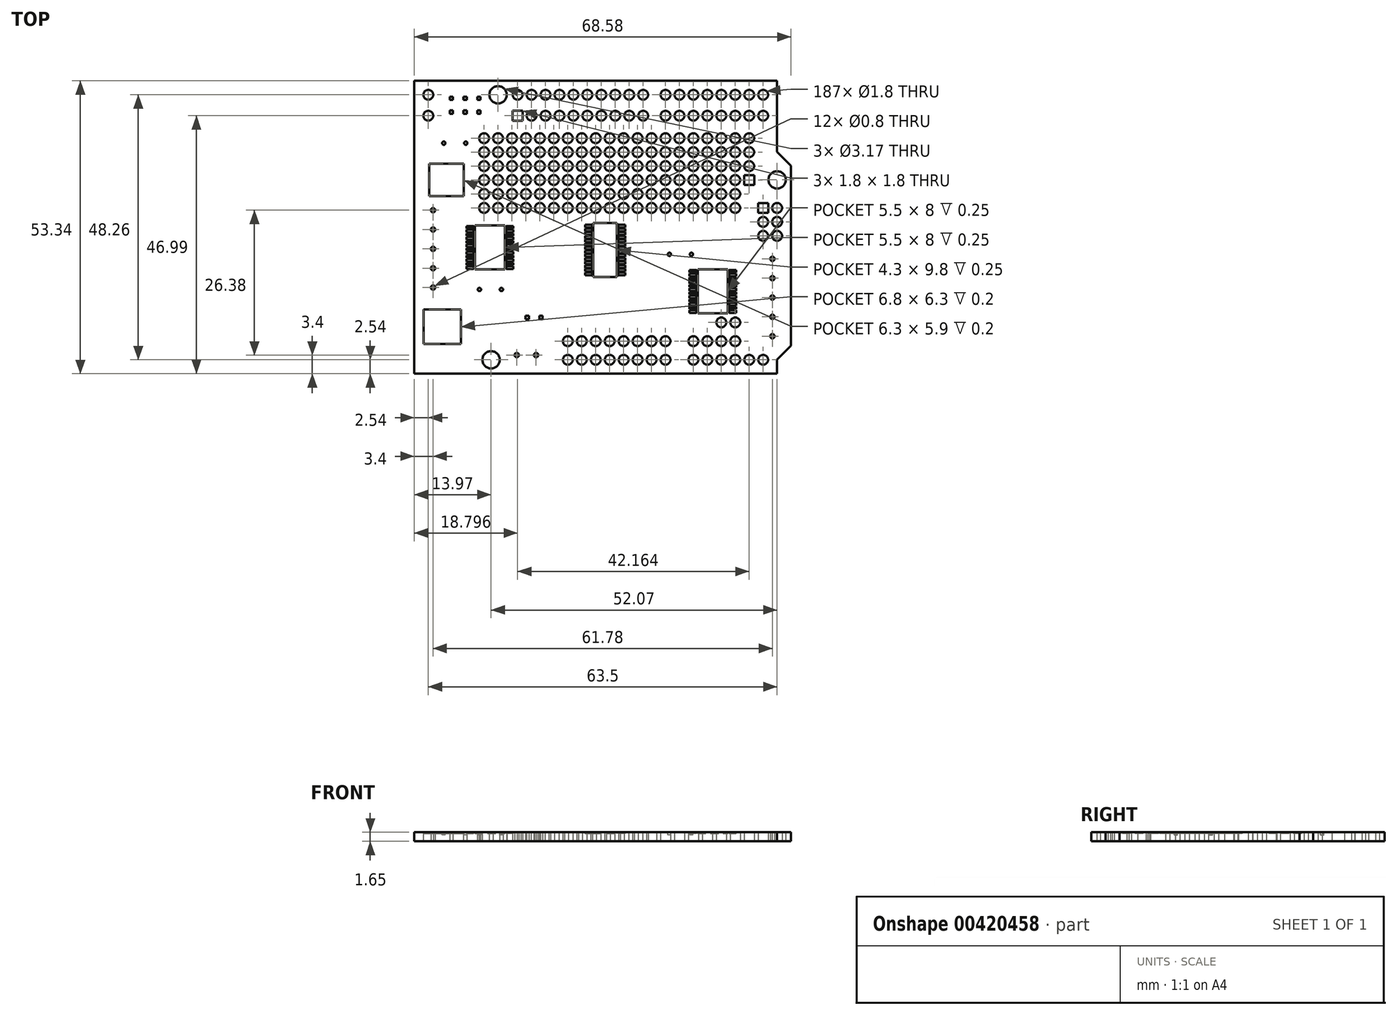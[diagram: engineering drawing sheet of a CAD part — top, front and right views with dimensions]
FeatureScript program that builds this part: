
annotation { "Feature Type Name" : "Feature", "Feature Type Description" : "" }
export const myFeature = defineFeature(function(context is Context, id is Id, definition is map)
    precondition{}
    {
        {
            var Q0;
            Q0=qCreatedBy(makeId("Top.planeOp"),FACE);
            var sketch = newSketch(context, id + "F0", { "sketchPlane" : qUnion([Q0])});
            skLineSegment(sketch, "E0.bottom", {"start": v(0, 0) * mm, "end": v(66.04, 0) * mm});
            skLineSegment(sketch, "E0.top", {"start": v(0, 53.34) * mm, "end": v(66.04, 53.34) * mm});
            skLineSegment(sketch, "E0.left", {"start": v(0, 0) * mm, "end": v(0, 53.34) * mm});
            skLineSegment(sketch, "E0.right", {"start": v(66.04, 0) * mm, "end": v(66.04, 2.54) * mm});
            skLineSegment(sketch, "E1", {"start": v(66.04, 40.39) * mm, "end": v(68.58, 37.85) * mm});
            skLineSegment(sketch, "E2", {"start": v(68.58, 37.85) * mm, "end": v(68.58, 5.08) * mm});
            skLineSegment(sketch, "E3", {"start": v(68.58, 5.08) * mm, "end": v(66.04, 2.54) * mm});
            skLineSegment(sketch, "E4.trimOffspring", {"start": v(66.04, 40.39) * mm, "end": v(66.04, 53.34) * mm});
            skCircle(sketch, "E5", {"center": v(15.24, 50.8) * mm, "radius": 1.59 * mm});
            skCircle(sketch, "E6", {"center": v(13.97, 2.54) * mm, "radius": 1.59 * mm});
            skCircle(sketch, "E7", {"center": v(66.04, 35.3) * mm, "radius": 1.59 * mm});
            skLineSegment(sketch, "E8", {"start": v(0, 50.8) * mm, "end": v(66.04, 50.8) * mm, "construction": true});
            skCircle(sketch, "E9", {"center": v(63.5, 50.8) * mm, "radius": 0.9 * mm});
            skCircle(sketch, "E10.1.0.0", {"center": v(60.96, 50.8) * mm, "radius": 0.9 * mm});
            skCircle(sketch, "E10.2.0.0", {"center": v(58.42, 50.8) * mm, "radius": 0.9 * mm});
            skCircle(sketch, "E10.3.0.0", {"center": v(55.88, 50.8) * mm, "radius": 0.9 * mm});
            skCircle(sketch, "E10.4.0.0", {"center": v(53.34, 50.8) * mm, "radius": 0.9 * mm});
            skCircle(sketch, "E10.5.0.0", {"center": v(50.8, 50.8) * mm, "radius": 0.9 * mm});
            skCircle(sketch, "E10.6.0.0", {"center": v(48.26, 50.8) * mm, "radius": 0.9 * mm});
            skCircle(sketch, "E10.7.0.0", {"center": v(45.72, 50.8) * mm, "radius": 0.9 * mm});
            skLineSegment(sketch, "E10.direction1", {"start": v(63.5, 50.8) * mm, "end": v(60.96, 50.8) * mm, "construction": true});
            skCircle(sketch, "E11", {"center": v(41.66, 50.8) * mm, "radius": 0.9 * mm});
            skCircle(sketch, "E12.1.0.0", {"center": v(39.12, 50.8) * mm, "radius": 0.9 * mm});
            skCircle(sketch, "E12.2.0.0", {"center": v(36.58, 50.8) * mm, "radius": 0.9 * mm});
            skCircle(sketch, "E12.3.0.0", {"center": v(34.04, 50.8) * mm, "radius": 0.9 * mm});
            skCircle(sketch, "E12.4.0.0", {"center": v(31.5, 50.8) * mm, "radius": 0.9 * mm});
            skCircle(sketch, "E12.5.0.0", {"center": v(28.96, 50.8) * mm, "radius": 0.9 * mm});
            skCircle(sketch, "E12.6.0.0", {"center": v(26.42, 50.8) * mm, "radius": 0.9 * mm});
            skCircle(sketch, "E12.7.0.0", {"center": v(23.88, 50.8) * mm, "radius": 0.9 * mm});
            skCircle(sketch, "E12.8.0.0", {"center": v(21.34, 50.8) * mm, "radius": 0.9 * mm});
            skCircle(sketch, "E12.9.0.0", {"center": v(18.8, 50.8) * mm, "radius": 0.9 * mm});
            skLineSegment(sketch, "E12.direction1", {"start": v(41.66, 50.8) * mm, "end": v(39.12, 50.8) * mm, "construction": true});
            skLineSegment(sketch, "E13", {"start": v(66.04, 2.54) * mm, "end": v(0, 2.54) * mm, "construction": true});
            skCircle(sketch, "E14", {"center": v(63.5, 2.54) * mm, "radius": 0.9 * mm});
            skCircle(sketch, "E15.1.0.0", {"center": v(60.96, 2.54) * mm, "radius": 0.9 * mm});
            skCircle(sketch, "E15.2.0.0", {"center": v(58.42, 2.54) * mm, "radius": 0.9 * mm});
            skCircle(sketch, "E15.3.0.0", {"center": v(55.88, 2.54) * mm, "radius": 0.9 * mm});
            skCircle(sketch, "E15.4.0.0", {"center": v(53.34, 2.54) * mm, "radius": 0.9 * mm});
            skCircle(sketch, "E15.5.0.0", {"center": v(50.8, 2.54) * mm, "radius": 0.9 * mm});
            skLineSegment(sketch, "E15.direction1", {"start": v(63.5, 2.54) * mm, "end": v(60.96, 2.54) * mm, "construction": true});
            skCircle(sketch, "E16", {"center": v(45.72, 2.54) * mm, "radius": 0.9 * mm});
            skCircle(sketch, "E17.1.0.0", {"center": v(43.18, 2.54) * mm, "radius": 0.9 * mm});
            skCircle(sketch, "E17.2.0.0", {"center": v(40.64, 2.54) * mm, "radius": 0.9 * mm});
            skCircle(sketch, "E17.3.0.0", {"center": v(38.1, 2.54) * mm, "radius": 0.9 * mm});
            skCircle(sketch, "E17.4.0.0", {"center": v(35.56, 2.54) * mm, "radius": 0.9 * mm});
            skCircle(sketch, "E17.5.0.0", {"center": v(33.02, 2.54) * mm, "radius": 0.9 * mm});
            skCircle(sketch, "E17.6.0.0", {"center": v(30.48, 2.54) * mm, "radius": 0.9 * mm});
            skCircle(sketch, "E17.7.0.0", {"center": v(27.94, 2.54) * mm, "radius": 0.9 * mm});
            skLineSegment(sketch, "E17.direction1", {"start": v(45.72, 2.54) * mm, "end": v(43.18, 2.54) * mm, "construction": true});
            skLineSegment(sketch, "E18", {"start": v(0, 46.99) * mm, "end": v(66.04, 46.99) * mm, "construction": true});
            skLineSegment(sketch, "E19.1.0.0", {"start": v(41.66, 46.99) * mm, "end": v(39.12, 46.99) * mm, "construction": true});
            skLineSegment(sketch, "E19.1.0.1", {"start": v(63.5, 46.99) * mm, "end": v(60.96, 46.99) * mm, "construction": true});
            skCircle(sketch, "E19.1.0.2", {"center": v(48.26, 46.99) * mm, "radius": 0.9 * mm});
            skCircle(sketch, "E19.1.0.3", {"center": v(31.5, 47) * mm, "radius": 0.9 * mm});
            skCircle(sketch, "E19.1.0.4", {"center": v(50.8, 46.99) * mm, "radius": 0.9 * mm});
            skCircle(sketch, "E19.1.0.6", {"center": v(34.04, 47) * mm, "radius": 0.9 * mm});
            skCircle(sketch, "E19.1.0.7", {"center": v(23.88, 47) * mm, "radius": 0.9 * mm});
            skCircle(sketch, "E19.1.0.8", {"center": v(53.34, 46.99) * mm, "radius": 0.9 * mm});
            skCircle(sketch, "E19.1.0.9", {"center": v(21.34, 46.99) * mm, "radius": 0.9 * mm});
            skCircle(sketch, "E19.1.0.10", {"center": v(36.58, 47) * mm, "radius": 0.9 * mm});
            skCircle(sketch, "E19.1.0.11", {"center": v(26.42, 47) * mm, "radius": 0.9 * mm});
            skCircle(sketch, "E19.1.0.12", {"center": v(55.88, 47) * mm, "radius": 0.9 * mm});
            skCircle(sketch, "E19.1.0.13", {"center": v(58.42, 47) * mm, "radius": 0.9 * mm});
            skCircle(sketch, "E19.1.0.14", {"center": v(45.72, 46.99) * mm, "radius": 0.9 * mm});
            skCircle(sketch, "E19.1.0.15", {"center": v(28.96, 47) * mm, "radius": 0.9 * mm});
            skCircle(sketch, "E19.1.0.16", {"center": v(39.12, 47) * mm, "radius": 0.9 * mm});
            skCircle(sketch, "E19.1.0.17", {"center": v(41.66, 47) * mm, "radius": 0.9 * mm});
            skCircle(sketch, "E19.1.0.18", {"center": v(63.5, 47) * mm, "radius": 0.9 * mm});
            skCircle(sketch, "E19.1.0.19", {"center": v(60.96, 47) * mm, "radius": 0.9 * mm});
            skLineSegment(sketch, "E19.direction1", {"start": v(18.8, 50.8) * mm, "end": v(18.8, 46.99) * mm, "construction": true});
            skLineSegment(sketch, "E20", {"start": v(68.58, 5.94) * mm, "end": v(0, 5.94) * mm, "construction": true});
            skLineSegment(sketch, "E21.1.0.0", {"start": v(45.72, 5.94) * mm, "end": v(43.18, 5.94) * mm, "construction": true});
            skCircle(sketch, "E21.1.0.1", {"center": v(55.88, 5.94) * mm, "radius": 0.9 * mm});
            skCircle(sketch, "E21.1.0.2", {"center": v(40.64, 5.94) * mm, "radius": 0.9 * mm});
            skCircle(sketch, "E21.1.0.3", {"center": v(58.42, 5.94) * mm, "radius": 0.9 * mm});
            skCircle(sketch, "E21.1.0.4", {"center": v(38.1, 5.94) * mm, "radius": 0.9 * mm});
            skCircle(sketch, "E21.1.0.5", {"center": v(30.48, 5.94) * mm, "radius": 0.9 * mm});
            skCircle(sketch, "E21.1.0.6", {"center": v(33.02, 5.94) * mm, "radius": 0.9 * mm});
            skCircle(sketch, "E21.1.0.7", {"center": v(50.8, 5.94) * mm, "radius": 0.9 * mm});
            skCircle(sketch, "E21.1.0.8", {"center": v(35.56, 5.94) * mm, "radius": 0.9 * mm});
            skCircle(sketch, "E21.1.0.9", {"center": v(53.34, 5.94) * mm, "radius": 0.9 * mm});
            skCircle(sketch, "E21.1.0.10", {"center": v(27.94, 5.94) * mm, "radius": 0.9 * mm});
            skCircle(sketch, "E21.1.0.11", {"center": v(43.18, 5.94) * mm, "radius": 0.9 * mm});
            skCircle(sketch, "E21.1.0.12", {"center": v(45.72, 5.94) * mm, "radius": 0.9 * mm});
            skLineSegment(sketch, "E21.direction1", {"start": v(27.94, 2.54) * mm, "end": v(27.94, 5.94) * mm, "construction": true});
            skLineSegment(sketch, "E22", {"start": v(58.42, 47) * mm, "end": v(58.42, 5.94) * mm, "construction": true});
            skLineSegment(sketch, "E23", {"start": v(0, 30.2) * mm, "end": v(66.04, 30.2) * mm, "construction": true});
            skLineSegment(sketch, "E24", {"start": v(0, 42.9) * mm, "end": v(66.04, 42.9) * mm, "construction": true});
            skCircle(sketch, "E25", {"center": v(58.42, 42.9) * mm, "radius": 0.9 * mm});
            skCircle(sketch, "E26", {"center": v(58.42, 30.2) * mm, "radius": 0.9 * mm});
            skCircle(sketch, "E27", {"center": v(58.42, 40.36) * mm, "radius": 0.9 * mm});
            skCircle(sketch, "E28", {"center": v(58.42, 37.82) * mm, "radius": 0.9 * mm});
            skCircle(sketch, "E29", {"center": v(58.42, 35.28) * mm, "radius": 0.9 * mm});
            skCircle(sketch, "E30", {"center": v(58.42, 32.74) * mm, "radius": 0.9 * mm});
            skCircle(sketch, "E31.1.0.0", {"center": v(55.88, 35.28) * mm, "radius": 0.9 * mm});
            skCircle(sketch, "E31.1.0.1", {"center": v(55.88, 32.74) * mm, "radius": 0.9 * mm});
            skCircle(sketch, "E31.1.0.2", {"center": v(55.88, 37.82) * mm, "radius": 0.9 * mm});
            skCircle(sketch, "E31.1.0.3", {"center": v(55.88, 40.36) * mm, "radius": 0.9 * mm});
            skCircle(sketch, "E31.1.0.4", {"center": v(55.88, 30.2) * mm, "radius": 0.9 * mm});
            skCircle(sketch, "E31.1.0.5", {"center": v(55.88, 42.9) * mm, "radius": 0.9 * mm});
            skCircle(sketch, "E31.2.0.0", {"center": v(53.34, 35.28) * mm, "radius": 0.9 * mm});
            skCircle(sketch, "E31.2.0.1", {"center": v(53.34, 32.74) * mm, "radius": 0.9 * mm});
            skCircle(sketch, "E31.2.0.2", {"center": v(53.34, 37.82) * mm, "radius": 0.9 * mm});
            skCircle(sketch, "E31.2.0.3", {"center": v(53.34, 40.36) * mm, "radius": 0.9 * mm});
            skCircle(sketch, "E31.2.0.4", {"center": v(53.34, 30.2) * mm, "radius": 0.9 * mm});
            skCircle(sketch, "E31.2.0.5", {"center": v(53.34, 42.9) * mm, "radius": 0.9 * mm});
            skCircle(sketch, "E31.3.0.0", {"center": v(50.8, 35.28) * mm, "radius": 0.9 * mm});
            skCircle(sketch, "E31.3.0.1", {"center": v(50.8, 32.74) * mm, "radius": 0.9 * mm});
            skCircle(sketch, "E31.3.0.2", {"center": v(50.8, 37.82) * mm, "radius": 0.9 * mm});
            skCircle(sketch, "E31.3.0.3", {"center": v(50.8, 40.36) * mm, "radius": 0.9 * mm});
            skCircle(sketch, "E31.3.0.4", {"center": v(50.8, 30.2) * mm, "radius": 0.9 * mm});
            skCircle(sketch, "E31.3.0.5", {"center": v(50.8, 42.9) * mm, "radius": 0.9 * mm});
            skCircle(sketch, "E31.4.0.0", {"center": v(48.26, 35.28) * mm, "radius": 0.9 * mm});
            skCircle(sketch, "E31.4.0.1", {"center": v(48.26, 32.74) * mm, "radius": 0.9 * mm});
            skCircle(sketch, "E31.4.0.2", {"center": v(48.26, 37.82) * mm, "radius": 0.9 * mm});
            skCircle(sketch, "E31.4.0.3", {"center": v(48.26, 40.36) * mm, "radius": 0.9 * mm});
            skCircle(sketch, "E31.4.0.4", {"center": v(48.26, 30.2) * mm, "radius": 0.9 * mm});
            skCircle(sketch, "E31.4.0.5", {"center": v(48.26, 42.9) * mm, "radius": 0.9 * mm});
            skCircle(sketch, "E31.5.0.0", {"center": v(45.72, 35.28) * mm, "radius": 0.9 * mm});
            skCircle(sketch, "E31.5.0.1", {"center": v(45.72, 32.74) * mm, "radius": 0.9 * mm});
            skCircle(sketch, "E31.5.0.2", {"center": v(45.72, 37.82) * mm, "radius": 0.9 * mm});
            skCircle(sketch, "E31.5.0.3", {"center": v(45.72, 40.36) * mm, "radius": 0.9 * mm});
            skCircle(sketch, "E31.5.0.4", {"center": v(45.72, 30.2) * mm, "radius": 0.9 * mm});
            skCircle(sketch, "E31.5.0.5", {"center": v(45.72, 42.9) * mm, "radius": 0.9 * mm});
            skCircle(sketch, "E31.6.0.0", {"center": v(43.18, 35.28) * mm, "radius": 0.9 * mm});
            skCircle(sketch, "E31.6.0.1", {"center": v(43.18, 32.74) * mm, "radius": 0.9 * mm});
            skCircle(sketch, "E31.6.0.2", {"center": v(43.18, 37.82) * mm, "radius": 0.9 * mm});
            skCircle(sketch, "E31.6.0.3", {"center": v(43.18, 40.36) * mm, "radius": 0.9 * mm});
            skCircle(sketch, "E31.6.0.4", {"center": v(43.18, 30.2) * mm, "radius": 0.9 * mm});
            skCircle(sketch, "E31.6.0.5", {"center": v(43.18, 42.9) * mm, "radius": 0.9 * mm});
            skCircle(sketch, "E31.7.0.0", {"center": v(40.64, 35.28) * mm, "radius": 0.9 * mm});
            skCircle(sketch, "E31.7.0.1", {"center": v(40.64, 32.74) * mm, "radius": 0.9 * mm});
            skCircle(sketch, "E31.7.0.2", {"center": v(40.64, 37.82) * mm, "radius": 0.9 * mm});
            skCircle(sketch, "E31.7.0.3", {"center": v(40.64, 40.36) * mm, "radius": 0.9 * mm});
            skCircle(sketch, "E31.7.0.4", {"center": v(40.64, 30.2) * mm, "radius": 0.9 * mm});
            skCircle(sketch, "E31.7.0.5", {"center": v(40.64, 42.9) * mm, "radius": 0.9 * mm});
            skCircle(sketch, "E31.8.0.0", {"center": v(38.1, 35.28) * mm, "radius": 0.9 * mm});
            skCircle(sketch, "E31.8.0.1", {"center": v(38.1, 32.74) * mm, "radius": 0.9 * mm});
            skCircle(sketch, "E31.8.0.2", {"center": v(38.1, 37.82) * mm, "radius": 0.9 * mm});
            skCircle(sketch, "E31.8.0.3", {"center": v(38.1, 40.36) * mm, "radius": 0.9 * mm});
            skCircle(sketch, "E31.8.0.4", {"center": v(38.1, 30.2) * mm, "radius": 0.9 * mm});
            skCircle(sketch, "E31.8.0.5", {"center": v(38.1, 42.9) * mm, "radius": 0.9 * mm});
            skCircle(sketch, "E31.9.0.0", {"center": v(35.56, 35.28) * mm, "radius": 0.9 * mm});
            skCircle(sketch, "E31.9.0.1", {"center": v(35.56, 32.74) * mm, "radius": 0.9 * mm});
            skCircle(sketch, "E31.9.0.2", {"center": v(35.56, 37.82) * mm, "radius": 0.9 * mm});
            skCircle(sketch, "E31.9.0.3", {"center": v(35.56, 40.36) * mm, "radius": 0.9 * mm});
            skCircle(sketch, "E31.9.0.4", {"center": v(35.56, 30.2) * mm, "radius": 0.9 * mm});
            skCircle(sketch, "E31.9.0.5", {"center": v(35.56, 42.9) * mm, "radius": 0.9 * mm});
            skCircle(sketch, "E31.10.0.0", {"center": v(33.02, 35.28) * mm, "radius": 0.9 * mm});
            skCircle(sketch, "E31.10.0.1", {"center": v(33.02, 32.74) * mm, "radius": 0.9 * mm});
            skCircle(sketch, "E31.10.0.2", {"center": v(33.02, 37.82) * mm, "radius": 0.9 * mm});
            skCircle(sketch, "E31.10.0.3", {"center": v(33.02, 40.36) * mm, "radius": 0.9 * mm});
            skCircle(sketch, "E31.10.0.4", {"center": v(33.02, 30.2) * mm, "radius": 0.9 * mm});
            skCircle(sketch, "E31.10.0.5", {"center": v(33.02, 42.9) * mm, "radius": 0.9 * mm});
            skCircle(sketch, "E31.11.0.0", {"center": v(30.48, 35.28) * mm, "radius": 0.9 * mm});
            skCircle(sketch, "E31.11.0.1", {"center": v(30.48, 32.74) * mm, "radius": 0.9 * mm});
            skCircle(sketch, "E31.11.0.2", {"center": v(30.48, 37.82) * mm, "radius": 0.9 * mm});
            skCircle(sketch, "E31.11.0.3", {"center": v(30.48, 40.36) * mm, "radius": 0.9 * mm});
            skCircle(sketch, "E31.11.0.4", {"center": v(30.48, 30.2) * mm, "radius": 0.9 * mm});
            skCircle(sketch, "E31.11.0.5", {"center": v(30.48, 42.9) * mm, "radius": 0.9 * mm});
            skCircle(sketch, "E31.12.0.0", {"center": v(27.94, 35.28) * mm, "radius": 0.9 * mm});
            skCircle(sketch, "E31.12.0.1", {"center": v(27.94, 32.74) * mm, "radius": 0.9 * mm});
            skCircle(sketch, "E31.12.0.2", {"center": v(27.94, 37.82) * mm, "radius": 0.9 * mm});
            skCircle(sketch, "E31.12.0.3", {"center": v(27.94, 40.36) * mm, "radius": 0.9 * mm});
            skCircle(sketch, "E31.12.0.4", {"center": v(27.94, 30.2) * mm, "radius": 0.9 * mm});
            skCircle(sketch, "E31.12.0.5", {"center": v(27.94, 42.9) * mm, "radius": 0.9 * mm});
            skCircle(sketch, "E31.13.0.0", {"center": v(25.4, 35.28) * mm, "radius": 0.9 * mm});
            skCircle(sketch, "E31.13.0.1", {"center": v(25.4, 32.74) * mm, "radius": 0.9 * mm});
            skCircle(sketch, "E31.13.0.2", {"center": v(25.4, 37.82) * mm, "radius": 0.9 * mm});
            skCircle(sketch, "E31.13.0.3", {"center": v(25.4, 40.36) * mm, "radius": 0.9 * mm});
            skCircle(sketch, "E31.13.0.4", {"center": v(25.4, 30.2) * mm, "radius": 0.9 * mm});
            skCircle(sketch, "E31.13.0.5", {"center": v(25.4, 42.9) * mm, "radius": 0.9 * mm});
            skCircle(sketch, "E31.14.0.0", {"center": v(22.86, 35.28) * mm, "radius": 0.9 * mm});
            skCircle(sketch, "E31.14.0.1", {"center": v(22.86, 32.74) * mm, "radius": 0.9 * mm});
            skCircle(sketch, "E31.14.0.2", {"center": v(22.86, 37.82) * mm, "radius": 0.9 * mm});
            skCircle(sketch, "E31.14.0.3", {"center": v(22.86, 40.36) * mm, "radius": 0.9 * mm});
            skCircle(sketch, "E31.14.0.4", {"center": v(22.86, 30.2) * mm, "radius": 0.9 * mm});
            skCircle(sketch, "E31.14.0.5", {"center": v(22.86, 42.9) * mm, "radius": 0.9 * mm});
            skCircle(sketch, "E31.15.0.0", {"center": v(20.32, 35.28) * mm, "radius": 0.9 * mm});
            skCircle(sketch, "E31.15.0.1", {"center": v(20.32, 32.74) * mm, "radius": 0.9 * mm});
            skCircle(sketch, "E31.15.0.2", {"center": v(20.32, 37.82) * mm, "radius": 0.9 * mm});
            skCircle(sketch, "E31.15.0.3", {"center": v(20.32, 40.36) * mm, "radius": 0.9 * mm});
            skCircle(sketch, "E31.15.0.4", {"center": v(20.32, 30.2) * mm, "radius": 0.9 * mm});
            skCircle(sketch, "E31.15.0.5", {"center": v(20.32, 42.9) * mm, "radius": 0.9 * mm});
            skCircle(sketch, "E31.16.0.0", {"center": v(17.78, 35.28) * mm, "radius": 0.9 * mm});
            skCircle(sketch, "E31.16.0.1", {"center": v(17.78, 32.74) * mm, "radius": 0.9 * mm});
            skCircle(sketch, "E31.16.0.2", {"center": v(17.78, 37.82) * mm, "radius": 0.9 * mm});
            skCircle(sketch, "E31.16.0.3", {"center": v(17.78, 40.36) * mm, "radius": 0.9 * mm});
            skCircle(sketch, "E31.16.0.4", {"center": v(17.78, 30.2) * mm, "radius": 0.9 * mm});
            skCircle(sketch, "E31.16.0.5", {"center": v(17.78, 42.9) * mm, "radius": 0.9 * mm});
            skCircle(sketch, "E31.17.0.0", {"center": v(15.24, 35.28) * mm, "radius": 0.9 * mm});
            skCircle(sketch, "E31.17.0.1", {"center": v(15.24, 32.74) * mm, "radius": 0.9 * mm});
            skCircle(sketch, "E31.17.0.2", {"center": v(15.24, 37.82) * mm, "radius": 0.9 * mm});
            skCircle(sketch, "E31.17.0.3", {"center": v(15.24, 40.36) * mm, "radius": 0.9 * mm});
            skCircle(sketch, "E31.17.0.4", {"center": v(15.24, 30.2) * mm, "radius": 0.9 * mm});
            skCircle(sketch, "E31.17.0.5", {"center": v(15.24, 42.9) * mm, "radius": 0.9 * mm});
            skCircle(sketch, "E31.18.0.0", {"center": v(12.7, 35.28) * mm, "radius": 0.9 * mm});
            skCircle(sketch, "E31.18.0.1", {"center": v(12.7, 32.74) * mm, "radius": 0.9 * mm});
            skCircle(sketch, "E31.18.0.2", {"center": v(12.7, 37.82) * mm, "radius": 0.9 * mm});
            skCircle(sketch, "E31.18.0.3", {"center": v(12.7, 40.36) * mm, "radius": 0.9 * mm});
            skCircle(sketch, "E31.18.0.4", {"center": v(12.7, 30.2) * mm, "radius": 0.9 * mm});
            skCircle(sketch, "E31.18.0.5", {"center": v(12.7, 42.9) * mm, "radius": 0.9 * mm});
            skLineSegment(sketch, "E31.direction1", {"start": v(58.42, 30.2) * mm, "end": v(55.88, 30.2) * mm, "construction": true});
            skCircle(sketch, "E32", {"center": v(60.96, 42.9) * mm, "radius": 0.9 * mm});
            skCircle(sketch, "E33", {"center": v(60.96, 40.36) * mm, "radius": 0.9 * mm});
            skCircle(sketch, "E34", {"center": v(60.96, 37.82) * mm, "radius": 0.9 * mm});
            skLineSegment(sketch, "E35", {"start": v(66.04, 40.39) * mm, "end": v(66.04, 2.54) * mm, "construction": true});
            skCircle(sketch, "E36", {"center": v(66.04, 25.12) * mm, "radius": 0.9 * mm});
            skCircle(sketch, "E37", {"center": v(66.04, 30.2) * mm, "radius": 0.9 * mm});
            skCircle(sketch, "E38", {"center": v(66.04, 27.66) * mm, "radius": 0.9 * mm});
            skCircle(sketch, "E39", {"center": v(63.5, 27.66) * mm, "radius": 0.9 * mm});
            skCircle(sketch, "E40", {"center": v(63.5, 25.12) * mm, "radius": 0.9 * mm});
            skCircle(sketch, "E41", {"center": v(58.42, 9.34) * mm, "radius": 0.9 * mm});
            skCircle(sketch, "E42", {"center": v(55.88, 9.34) * mm, "radius": 0.9 * mm});
            skCircle(sketch, "E43", {"center": v(2.54, 50.8) * mm, "radius": 0.9 * mm});
            skCircle(sketch, "E44", {"center": v(2.54, 46.99) * mm, "radius": 0.9 * mm});
            skLineSegment(sketch, "E45.bottom", {"start": v(17.9, 47.9) * mm, "end": v(19.7, 47.9) * mm});
            skLineSegment(sketch, "E45.top", {"start": v(17.9, 46.1) * mm, "end": v(19.7, 46.1) * mm});
            skLineSegment(sketch, "E45.left", {"start": v(17.9, 47.9) * mm, "end": v(17.9, 46.1) * mm});
            skLineSegment(sketch, "E45.right", {"start": v(19.7, 47.9) * mm, "end": v(19.7, 46.1) * mm});
            skLineSegment(sketch, "E46.bottom", {"start": v(60.06, 36.18) * mm, "end": v(61.86, 36.18) * mm});
            skLineSegment(sketch, "E46.top", {"start": v(60.06, 34.38) * mm, "end": v(61.86, 34.38) * mm});
            skLineSegment(sketch, "E46.left", {"start": v(60.06, 36.18) * mm, "end": v(60.06, 34.38) * mm});
            skLineSegment(sketch, "E46.right", {"start": v(61.86, 36.18) * mm, "end": v(61.86, 34.38) * mm});
            skLineSegment(sketch, "E47.bottom", {"start": v(62.6, 31.1) * mm, "end": v(64.4, 31.1) * mm});
            skLineSegment(sketch, "E47.top", {"start": v(62.6, 29.3) * mm, "end": v(64.4, 29.3) * mm});
            skLineSegment(sketch, "E47.left", {"start": v(62.6, 31.1) * mm, "end": v(62.6, 29.3) * mm});
            skLineSegment(sketch, "E47.right", {"start": v(64.4, 31.1) * mm, "end": v(64.4, 29.3) * mm});
            skLineSegment(sketch, "E48", {"start": v(68.58, 5.08) * mm, "end": v(61.78, 5.08) * mm, "construction": true});
            skLineSegment(sketch, "E49", {"start": v(61.78, 5.08) * mm, "end": v(61.78, 22.68) * mm, "construction": true});
            skLineSegment(sketch, "E50", {"start": v(61.78, 22.68) * mm, "end": v(68.58, 22.68) * mm, "construction": true});
            skLineSegment(sketch, "E51", {"start": v(61.78, 20.92) * mm, "end": v(68.58, 20.92) * mm, "construction": true});
            skLineSegment(sketch, "E52", {"start": v(61.78, 17.4) * mm, "end": v(68.58, 17.4) * mm, "construction": true});
            skLineSegment(sketch, "E53", {"start": v(61.78, 13.88) * mm, "end": v(68.58, 13.88) * mm, "construction": true});
            skLineSegment(sketch, "E54", {"start": v(61.78, 10.36) * mm, "end": v(68.58, 10.36) * mm, "construction": true});
            skLineSegment(sketch, "E55", {"start": v(61.78, 6.84) * mm, "end": v(68.58, 6.84) * mm, "construction": true});
            skCircle(sketch, "E56", {"center": v(65.18, 17.4) * mm, "radius": 0.4 * mm});
            skCircle(sketch, "E57", {"center": v(65.18, 20.92) * mm, "radius": 0.4 * mm});
            skCircle(sketch, "E58", {"center": v(65.18, 13.88) * mm, "radius": 0.4 * mm});
            skCircle(sketch, "E59", {"center": v(65.18, 10.36) * mm, "radius": 0.4 * mm});
            skCircle(sketch, "E60", {"center": v(65.18, 6.84) * mm, "radius": 0.4 * mm});
            skLineSegment(sketch, "E61", {"start": v(0, 31.54) * mm, "end": v(6.8, 31.54) * mm, "construction": true});
            skLineSegment(sketch, "E62", {"start": v(6.8, 31.54) * mm, "end": v(6.8, 13.94) * mm, "construction": true});
            skLineSegment(sketch, "E63", {"start": v(6.8, 13.94) * mm, "end": v(0, 13.94) * mm, "construction": true});
            skLineSegment(sketch, "E64", {"start": v(0, 29.78) * mm, "end": v(6.8, 29.78) * mm, "construction": true});
            skLineSegment(sketch, "E65", {"start": v(0, 26.26) * mm, "end": v(6.8, 26.26) * mm, "construction": true});
            skLineSegment(sketch, "E66", {"start": v(0, 22.74) * mm, "end": v(6.8, 22.74) * mm, "construction": true});
            skLineSegment(sketch, "E67", {"start": v(0, 19.22) * mm, "end": v(6.8, 19.22) * mm, "construction": true});
            skLineSegment(sketch, "E68", {"start": v(0, 15.7) * mm, "end": v(6.8, 15.7) * mm, "construction": true});
            skCircle(sketch, "E69", {"center": v(3.4, 29.78) * mm, "radius": 0.4 * mm});
            skCircle(sketch, "E70", {"center": v(3.4, 26.26) * mm, "radius": 0.4 * mm});
            skCircle(sketch, "E71", {"center": v(3.4, 22.74) * mm, "radius": 0.4 * mm});
            skCircle(sketch, "E72", {"center": v(3.4, 19.22) * mm, "radius": 0.4 * mm});
            skCircle(sketch, "E73", {"center": v(3.4, 15.7) * mm, "radius": 0.4 * mm});
            skLineSegment(sketch, "E74", {"start": v(16.88, 0) * mm, "end": v(16.88, 6.8) * mm, "construction": true});
            skLineSegment(sketch, "E75", {"start": v(16.88, 6.8) * mm, "end": v(23.92, 6.8) * mm, "construction": true});
            skLineSegment(sketch, "E76", {"start": v(23.92, 6.8) * mm, "end": v(23.92, 0) * mm, "construction": true});
            skLineSegment(sketch, "E77", {"start": v(18.64, 6.8) * mm, "end": v(18.64, 0) * mm, "construction": true});
            skLineSegment(sketch, "E78", {"start": v(22.16, 6.8) * mm, "end": v(22.16, 0) * mm, "construction": true});
            skCircle(sketch, "E79", {"center": v(18.64, 3.4) * mm, "radius": 0.4 * mm});
            skCircle(sketch, "E80", {"center": v(22.16, 3.4) * mm, "radius": 0.4 * mm});
            skLineSegment(sketch, "E81.bottom", {"start": v(5.5, 51.4) * mm, "end": v(13, 51.4) * mm, "construction": true});
            skLineSegment(sketch, "E81.top", {"start": v(5.5, 46.4) * mm, "end": v(13, 46.4) * mm, "construction": true});
            skLineSegment(sketch, "E81.left", {"start": v(5.5, 51.4) * mm, "end": v(5.5, 46.4) * mm, "construction": true});
            skLineSegment(sketch, "E81.right", {"start": v(13, 51.4) * mm, "end": v(13, 46.4) * mm, "construction": true});
            skLineSegment(sketch, "E82", {"start": v(6.75, 51.4) * mm, "end": v(6.75, 46.4) * mm, "construction": true});
            skLineSegment(sketch, "E83", {"start": v(11.75, 51.4) * mm, "end": v(11.75, 46.4) * mm, "construction": true});
            skLineSegment(sketch, "E84", {"start": v(9.25, 51.4) * mm, "end": v(9.25, 46.4) * mm, "construction": true});
            skLineSegment(sketch, "E85.bottom", {"start": v(6.45, 50.45) * mm, "end": v(7.05, 50.45) * mm});
            skLineSegment(sketch, "E85.top", {"start": v(6.45, 49.84) * mm, "end": v(7.05, 49.84) * mm});
            skLineSegment(sketch, "E85.left", {"start": v(6.45, 50.45) * mm, "end": v(6.45, 49.84) * mm});
            skLineSegment(sketch, "E85.right", {"start": v(7.05, 50.45) * mm, "end": v(7.05, 49.84) * mm});
            skLineSegment(sketch, "E86.bottom", {"start": v(8.95, 50.45) * mm, "end": v(9.55, 50.45) * mm});
            skLineSegment(sketch, "E86.top", {"start": v(8.95, 49.84) * mm, "end": v(9.55, 49.84) * mm});
            skLineSegment(sketch, "E86.left", {"start": v(8.95, 50.45) * mm, "end": v(8.95, 49.84) * mm});
            skLineSegment(sketch, "E86.right", {"start": v(9.55, 50.45) * mm, "end": v(9.55, 49.84) * mm});
            skLineSegment(sketch, "E87.bottom", {"start": v(11.45, 50.45) * mm, "end": v(12.05, 50.45) * mm});
            skLineSegment(sketch, "E87.top", {"start": v(11.45, 49.84) * mm, "end": v(12.05, 49.84) * mm});
            skLineSegment(sketch, "E87.left", {"start": v(11.45, 50.45) * mm, "end": v(11.45, 49.84) * mm});
            skLineSegment(sketch, "E87.right", {"start": v(12.05, 50.45) * mm, "end": v(12.05, 49.84) * mm});
            skLineSegment(sketch, "E88.bottom", {"start": v(6.45, 47.95) * mm, "end": v(7.05, 47.95) * mm});
            skLineSegment(sketch, "E88.top", {"start": v(6.45, 47.34) * mm, "end": v(7.05, 47.34) * mm});
            skLineSegment(sketch, "E88.left", {"start": v(6.45, 47.95) * mm, "end": v(6.45, 47.34) * mm});
            skLineSegment(sketch, "E88.right", {"start": v(7.05, 47.95) * mm, "end": v(7.05, 47.34) * mm});
            skLineSegment(sketch, "E89.bottom", {"start": v(8.95, 47.95) * mm, "end": v(9.55, 47.95) * mm});
            skLineSegment(sketch, "E89.top", {"start": v(8.95, 47.35) * mm, "end": v(9.55, 47.35) * mm});
            skLineSegment(sketch, "E89.left", {"start": v(8.95, 47.95) * mm, "end": v(8.95, 47.34) * mm});
            skLineSegment(sketch, "E89.right", {"start": v(9.55, 47.95) * mm, "end": v(9.55, 47.34) * mm});
            skLineSegment(sketch, "E90.bottom", {"start": v(11.45, 47.95) * mm, "end": v(12.05, 47.95) * mm});
            skLineSegment(sketch, "E90.top", {"start": v(11.45, 47.35) * mm, "end": v(12.05, 47.35) * mm});
            skLineSegment(sketch, "E90.left", {"start": v(11.45, 47.95) * mm, "end": v(11.45, 47.35) * mm});
            skLineSegment(sketch, "E90.right", {"start": v(12.05, 47.95) * mm, "end": v(12.05, 47.35) * mm});
            skLineSegment(sketch, "E91.bottom", {"start": v(19.3, 11.5) * mm, "end": v(24.3, 11.5) * mm, "construction": true});
            skLineSegment(sketch, "E91.top", {"start": v(19.3, 9) * mm, "end": v(24.3, 9) * mm, "construction": true});
            skLineSegment(sketch, "E91.left", {"start": v(19.3, 11.5) * mm, "end": v(19.3, 9) * mm, "construction": true});
            skLineSegment(sketch, "E91.right", {"start": v(24.3, 11.5) * mm, "end": v(24.3, 9) * mm, "construction": true});
            skLineSegment(sketch, "E92.bottom", {"start": v(20.25, 10.55) * mm, "end": v(20.85, 10.55) * mm});
            skLineSegment(sketch, "E92.top", {"start": v(20.25, 9.95) * mm, "end": v(20.85, 9.95) * mm});
            skLineSegment(sketch, "E92.left", {"start": v(20.25, 10.55) * mm, "end": v(20.25, 9.95) * mm});
            skLineSegment(sketch, "E92.right", {"start": v(20.85, 10.55) * mm, "end": v(20.85, 9.95) * mm});
            skLineSegment(sketch, "E93.bottom", {"start": v(22.75, 10.55) * mm, "end": v(23.35, 10.55) * mm});
            skLineSegment(sketch, "E93.top", {"start": v(22.75, 9.95) * mm, "end": v(23.35, 9.95) * mm});
            skLineSegment(sketch, "E93.left", {"start": v(22.75, 10.55) * mm, "end": v(22.75, 9.95) * mm});
            skLineSegment(sketch, "E93.right", {"start": v(23.35, 10.55) * mm, "end": v(23.35, 9.95) * mm});
            skSolve(sketch);
        }
        {
            var Q0;
            Q0 = qSketchRegion(id + "F0", true);
            extrude(context, id + "F1", {"entities" : qUnion([Q0]), "depth" : 1.65 * mm});
        }
        {
            var Q0;
            Q0=makeQuery(id+"F1.opExtrude","CAP_FACE",FACE,{"disambiguationData":[OSD([sQuery(id+"F0.wireOp",EDGE,"E0.bottom"),sQuery(id+"F0.wireOp",EDGE,"E0.top"),sQuery(id+"F0.wireOp",EDGE,"E0.left"),sQuery(id+"F0.wireOp",EDGE,"E0.right"),sQuery(id+"F0.wireOp",EDGE,"E1"),sQuery(id+"F0.wireOp",EDGE,"E2"),sQuery(id+"F0.wireOp",EDGE,"E3"),sQuery(id+"F0.wireOp",EDGE,"E4.trimOffspring"),sQuery(id+"F0.wireOp",EDGE,"E5"),sQuery(id+"F0.wireOp",EDGE,"E6"),sQuery(id+"F0.wireOp",EDGE,"E7"),sQuery(id+"F0.wireOp",EDGE,"E9"),sQuery(id+"F0.wireOp",EDGE,"E10.1.0.0"),sQuery(id+"F0.wireOp",EDGE,"E10.2.0.0"),sQuery(id+"F0.wireOp",EDGE,"E10.3.0.0"),sQuery(id+"F0.wireOp",EDGE,"E10.4.0.0"),sQuery(id+"F0.wireOp",EDGE,"E10.5.0.0"),sQuery(id+"F0.wireOp",EDGE,"E10.6.0.0"),sQuery(id+"F0.wireOp",EDGE,"E10.7.0.0"),sQuery(id+"F0.wireOp",EDGE,"E11"),sQuery(id+"F0.wireOp",EDGE,"E12.1.0.0"),sQuery(id+"F0.wireOp",EDGE,"E12.2.0.0"),sQuery(id+"F0.wireOp",EDGE,"E12.3.0.0"),sQuery(id+"F0.wireOp",EDGE,"E12.4.0.0"),sQuery(id+"F0.wireOp",EDGE,"E12.5.0.0"),sQuery(id+"F0.wireOp",EDGE,"E12.6.0.0"),sQuery(id+"F0.wireOp",EDGE,"E12.7.0.0"),sQuery(id+"F0.wireOp",EDGE,"E12.8.0.0"),sQuery(id+"F0.wireOp",EDGE,"E12.9.0.0"),sQuery(id+"F0.wireOp",EDGE,"E14"),sQuery(id+"F0.wireOp",EDGE,"E15.1.0.0"),sQuery(id+"F0.wireOp",EDGE,"E15.2.0.0"),sQuery(id+"F0.wireOp",EDGE,"E15.3.0.0"),sQuery(id+"F0.wireOp",EDGE,"E15.4.0.0"),sQuery(id+"F0.wireOp",EDGE,"E15.5.0.0"),sQuery(id+"F0.wireOp",EDGE,"E16"),sQuery(id+"F0.wireOp",EDGE,"E17.1.0.0"),sQuery(id+"F0.wireOp",EDGE,"E17.2.0.0"),sQuery(id+"F0.wireOp",EDGE,"E17.3.0.0"),sQuery(id+"F0.wireOp",EDGE,"E17.4.0.0"),sQuery(id+"F0.wireOp",EDGE,"E17.5.0.0"),sQuery(id+"F0.wireOp",EDGE,"E17.6.0.0"),sQuery(id+"F0.wireOp",EDGE,"E17.7.0.0"),sQuery(id+"F0.wireOp",EDGE,"E19.1.0.2"),sQuery(id+"F0.wireOp",EDGE,"E19.1.0.3"),sQuery(id+"F0.wireOp",EDGE,"E19.1.0.4"),sQuery(id+"F0.wireOp",EDGE,"E19.1.0.6"),sQuery(id+"F0.wireOp",EDGE,"E19.1.0.7"),sQuery(id+"F0.wireOp",EDGE,"E19.1.0.8"),sQuery(id+"F0.wireOp",EDGE,"E19.1.0.9"),sQuery(id+"F0.wireOp",EDGE,"E19.1.0.10"),sQuery(id+"F0.wireOp",EDGE,"E19.1.0.11"),sQuery(id+"F0.wireOp",EDGE,"E19.1.0.12"),sQuery(id+"F0.wireOp",EDGE,"E19.1.0.13"),sQuery(id+"F0.wireOp",EDGE,"E19.1.0.14"),sQuery(id+"F0.wireOp",EDGE,"E19.1.0.15"),sQuery(id+"F0.wireOp",EDGE,"E19.1.0.16"),sQuery(id+"F0.wireOp",EDGE,"E19.1.0.17"),sQuery(id+"F0.wireOp",EDGE,"E19.1.0.18"),sQuery(id+"F0.wireOp",EDGE,"E19.1.0.19"),sQuery(id+"F0.wireOp",EDGE,"E21.1.0.1"),sQuery(id+"F0.wireOp",EDGE,"E21.1.0.2"),sQuery(id+"F0.wireOp",EDGE,"E21.1.0.3"),sQuery(id+"F0.wireOp",EDGE,"E21.1.0.4"),sQuery(id+"F0.wireOp",EDGE,"E21.1.0.5"),sQuery(id+"F0.wireOp",EDGE,"E21.1.0.6"),sQuery(id+"F0.wireOp",EDGE,"E21.1.0.7"),sQuery(id+"F0.wireOp",EDGE,"E21.1.0.8"),sQuery(id+"F0.wireOp",EDGE,"E21.1.0.9"),sQuery(id+"F0.wireOp",EDGE,"E21.1.0.10"),sQuery(id+"F0.wireOp",EDGE,"E21.1.0.11"),sQuery(id+"F0.wireOp",EDGE,"E21.1.0.12"),sQuery(id+"F0.wireOp",EDGE,"E25"),sQuery(id+"F0.wireOp",EDGE,"E26"),sQuery(id+"F0.wireOp",EDGE,"E27"),sQuery(id+"F0.wireOp",EDGE,"E28"),sQuery(id+"F0.wireOp",EDGE,"E29"),sQuery(id+"F0.wireOp",EDGE,"E30"),sQuery(id+"F0.wireOp",EDGE,"E31.1.0.0"),sQuery(id+"F0.wireOp",EDGE,"E31.1.0.1"),sQuery(id+"F0.wireOp",EDGE,"E31.1.0.2"),sQuery(id+"F0.wireOp",EDGE,"E31.1.0.3"),sQuery(id+"F0.wireOp",EDGE,"E31.1.0.4"),sQuery(id+"F0.wireOp",EDGE,"E31.1.0.5"),sQuery(id+"F0.wireOp",EDGE,"E31.2.0.0"),sQuery(id+"F0.wireOp",EDGE,"E31.2.0.1"),sQuery(id+"F0.wireOp",EDGE,"E31.2.0.2"),sQuery(id+"F0.wireOp",EDGE,"E31.2.0.3"),sQuery(id+"F0.wireOp",EDGE,"E31.2.0.4"),sQuery(id+"F0.wireOp",EDGE,"E31.2.0.5"),sQuery(id+"F0.wireOp",EDGE,"E31.3.0.0"),sQuery(id+"F0.wireOp",EDGE,"E31.3.0.1"),sQuery(id+"F0.wireOp",EDGE,"E31.3.0.2"),sQuery(id+"F0.wireOp",EDGE,"E31.3.0.3"),sQuery(id+"F0.wireOp",EDGE,"E31.3.0.4"),sQuery(id+"F0.wireOp",EDGE,"E31.3.0.5"),sQuery(id+"F0.wireOp",EDGE,"E31.4.0.0"),sQuery(id+"F0.wireOp",EDGE,"E31.4.0.1"),sQuery(id+"F0.wireOp",EDGE,"E31.4.0.2"),sQuery(id+"F0.wireOp",EDGE,"E31.4.0.3"),sQuery(id+"F0.wireOp",EDGE,"E31.4.0.4"),sQuery(id+"F0.wireOp",EDGE,"E31.4.0.5"),sQuery(id+"F0.wireOp",EDGE,"E31.5.0.0"),sQuery(id+"F0.wireOp",EDGE,"E31.5.0.1"),sQuery(id+"F0.wireOp",EDGE,"E31.5.0.2"),sQuery(id+"F0.wireOp",EDGE,"E31.5.0.3"),sQuery(id+"F0.wireOp",EDGE,"E31.5.0.4"),sQuery(id+"F0.wireOp",EDGE,"E31.5.0.5"),sQuery(id+"F0.wireOp",EDGE,"E31.6.0.0"),sQuery(id+"F0.wireOp",EDGE,"E31.6.0.1"),sQuery(id+"F0.wireOp",EDGE,"E31.6.0.2"),sQuery(id+"F0.wireOp",EDGE,"E31.6.0.3"),sQuery(id+"F0.wireOp",EDGE,"E31.6.0.4"),sQuery(id+"F0.wireOp",EDGE,"E31.6.0.5"),sQuery(id+"F0.wireOp",EDGE,"E31.7.0.0"),sQuery(id+"F0.wireOp",EDGE,"E31.7.0.1"),sQuery(id+"F0.wireOp",EDGE,"E31.7.0.2"),sQuery(id+"F0.wireOp",EDGE,"E31.7.0.3"),sQuery(id+"F0.wireOp",EDGE,"E31.7.0.4"),sQuery(id+"F0.wireOp",EDGE,"E31.7.0.5"),sQuery(id+"F0.wireOp",EDGE,"E31.8.0.0"),sQuery(id+"F0.wireOp",EDGE,"E31.8.0.1"),sQuery(id+"F0.wireOp",EDGE,"E31.8.0.2"),sQuery(id+"F0.wireOp",EDGE,"E31.8.0.3"),sQuery(id+"F0.wireOp",EDGE,"E31.8.0.4"),sQuery(id+"F0.wireOp",EDGE,"E31.8.0.5"),sQuery(id+"F0.wireOp",EDGE,"E31.9.0.0"),sQuery(id+"F0.wireOp",EDGE,"E31.9.0.1"),sQuery(id+"F0.wireOp",EDGE,"E31.9.0.2"),sQuery(id+"F0.wireOp",EDGE,"E31.9.0.3"),sQuery(id+"F0.wireOp",EDGE,"E31.9.0.4"),sQuery(id+"F0.wireOp",EDGE,"E31.9.0.5"),sQuery(id+"F0.wireOp",EDGE,"E31.10.0.0"),sQuery(id+"F0.wireOp",EDGE,"E31.10.0.1"),sQuery(id+"F0.wireOp",EDGE,"E31.10.0.2"),sQuery(id+"F0.wireOp",EDGE,"E31.10.0.3"),sQuery(id+"F0.wireOp",EDGE,"E31.10.0.4"),sQuery(id+"F0.wireOp",EDGE,"E31.10.0.5"),sQuery(id+"F0.wireOp",EDGE,"E31.11.0.0"),sQuery(id+"F0.wireOp",EDGE,"E31.11.0.1"),sQuery(id+"F0.wireOp",EDGE,"E31.11.0.2"),sQuery(id+"F0.wireOp",EDGE,"E31.11.0.3"),sQuery(id+"F0.wireOp",EDGE,"E31.11.0.4"),sQuery(id+"F0.wireOp",EDGE,"E31.11.0.5"),sQuery(id+"F0.wireOp",EDGE,"E31.12.0.0"),sQuery(id+"F0.wireOp",EDGE,"E31.12.0.1"),sQuery(id+"F0.wireOp",EDGE,"E31.12.0.2"),sQuery(id+"F0.wireOp",EDGE,"E31.12.0.3"),sQuery(id+"F0.wireOp",EDGE,"E31.12.0.4"),sQuery(id+"F0.wireOp",EDGE,"E31.12.0.5"),sQuery(id+"F0.wireOp",EDGE,"E31.13.0.0"),sQuery(id+"F0.wireOp",EDGE,"E31.13.0.1"),sQuery(id+"F0.wireOp",EDGE,"E31.13.0.2"),sQuery(id+"F0.wireOp",EDGE,"E31.13.0.3"),sQuery(id+"F0.wireOp",EDGE,"E31.13.0.4"),sQuery(id+"F0.wireOp",EDGE,"E31.13.0.5"),sQuery(id+"F0.wireOp",EDGE,"E31.14.0.0"),sQuery(id+"F0.wireOp",EDGE,"E31.14.0.1"),sQuery(id+"F0.wireOp",EDGE,"E31.14.0.2"),sQuery(id+"F0.wireOp",EDGE,"E31.14.0.3"),sQuery(id+"F0.wireOp",EDGE,"E31.14.0.4"),sQuery(id+"F0.wireOp",EDGE,"E31.14.0.5"),sQuery(id+"F0.wireOp",EDGE,"E31.15.0.0"),sQuery(id+"F0.wireOp",EDGE,"E31.15.0.1"),sQuery(id+"F0.wireOp",EDGE,"E31.15.0.2"),sQuery(id+"F0.wireOp",EDGE,"E31.15.0.3"),sQuery(id+"F0.wireOp",EDGE,"E31.15.0.4"),sQuery(id+"F0.wireOp",EDGE,"E31.15.0.5"),sQuery(id+"F0.wireOp",EDGE,"E31.16.0.0"),sQuery(id+"F0.wireOp",EDGE,"E31.16.0.1"),sQuery(id+"F0.wireOp",EDGE,"E31.16.0.2"),sQuery(id+"F0.wireOp",EDGE,"E31.16.0.3"),sQuery(id+"F0.wireOp",EDGE,"E31.16.0.4"),sQuery(id+"F0.wireOp",EDGE,"E31.16.0.5"),sQuery(id+"F0.wireOp",EDGE,"E31.17.0.0"),sQuery(id+"F0.wireOp",EDGE,"E31.17.0.1"),sQuery(id+"F0.wireOp",EDGE,"E31.17.0.2"),sQuery(id+"F0.wireOp",EDGE,"E31.17.0.3"),sQuery(id+"F0.wireOp",EDGE,"E31.17.0.4"),sQuery(id+"F0.wireOp",EDGE,"E31.17.0.5"),sQuery(id+"F0.wireOp",EDGE,"E31.18.0.0"),sQuery(id+"F0.wireOp",EDGE,"E31.18.0.1"),sQuery(id+"F0.wireOp",EDGE,"E31.18.0.2"),sQuery(id+"F0.wireOp",EDGE,"E31.18.0.3"),sQuery(id+"F0.wireOp",EDGE,"E31.18.0.4"),sQuery(id+"F0.wireOp",EDGE,"E31.18.0.5"),sQuery(id+"F0.wireOp",EDGE,"E32"),sQuery(id+"F0.wireOp",EDGE,"E33"),sQuery(id+"F0.wireOp",EDGE,"E34"),sQuery(id+"F0.wireOp",EDGE,"E36"),sQuery(id+"F0.wireOp",EDGE,"E37"),sQuery(id+"F0.wireOp",EDGE,"E38"),sQuery(id+"F0.wireOp",EDGE,"E39"),sQuery(id+"F0.wireOp",EDGE,"E40"),sQuery(id+"F0.wireOp",EDGE,"E41"),sQuery(id+"F0.wireOp",EDGE,"E42"),sQuery(id+"F0.wireOp",EDGE,"E43"),sQuery(id+"F0.wireOp",EDGE,"E44"),sQuery(id+"F0.wireOp",EDGE,"E45.bottom"),sQuery(id+"F0.wireOp",EDGE,"E45.top"),sQuery(id+"F0.wireOp",EDGE,"E45.left"),sQuery(id+"F0.wireOp",EDGE,"E45.right"),sQuery(id+"F0.wireOp",EDGE,"E46.bottom"),sQuery(id+"F0.wireOp",EDGE,"E46.top"),sQuery(id+"F0.wireOp",EDGE,"E46.left"),sQuery(id+"F0.wireOp",EDGE,"E46.right"),sQuery(id+"F0.wireOp",EDGE,"E47.bottom"),sQuery(id+"F0.wireOp",EDGE,"E47.top"),sQuery(id+"F0.wireOp",EDGE,"E47.left"),sQuery(id+"F0.wireOp",EDGE,"E47.right"),sQuery(id+"F0.wireOp",EDGE,"E56"),sQuery(id+"F0.wireOp",EDGE,"E57"),sQuery(id+"F0.wireOp",EDGE,"E58"),sQuery(id+"F0.wireOp",EDGE,"E59"),sQuery(id+"F0.wireOp",EDGE,"E60"),sQuery(id+"F0.wireOp",EDGE,"E69"),sQuery(id+"F0.wireOp",EDGE,"E70"),sQuery(id+"F0.wireOp",EDGE,"E71"),sQuery(id+"F0.wireOp",EDGE,"E72"),sQuery(id+"F0.wireOp",EDGE,"E73"),sQuery(id+"F0.wireOp",EDGE,"E79"),sQuery(id+"F0.wireOp",EDGE,"E80"),sQuery(id+"F0.wireOp",EDGE,"E85.bottom"),sQuery(id+"F0.wireOp",EDGE,"E85.top"),sQuery(id+"F0.wireOp",EDGE,"E85.left"),sQuery(id+"F0.wireOp",EDGE,"E85.right"),sQuery(id+"F0.wireOp",EDGE,"E86.bottom"),sQuery(id+"F0.wireOp",EDGE,"E86.top"),sQuery(id+"F0.wireOp",EDGE,"E86.left"),sQuery(id+"F0.wireOp",EDGE,"E86.right"),sQuery(id+"F0.wireOp",EDGE,"E87.bottom"),sQuery(id+"F0.wireOp",EDGE,"E87.top"),sQuery(id+"F0.wireOp",EDGE,"E87.left"),sQuery(id+"F0.wireOp",EDGE,"E87.right"),sQuery(id+"F0.wireOp",EDGE,"E88.bottom"),sQuery(id+"F0.wireOp",EDGE,"E88.top"),sQuery(id+"F0.wireOp",EDGE,"E88.left"),sQuery(id+"F0.wireOp",EDGE,"E88.right"),sQuery(id+"F0.wireOp",EDGE,"E89.bottom"),sQuery(id+"F0.wireOp",EDGE,"E89.top"),sQuery(id+"F0.wireOp",EDGE,"E89.left"),sQuery(id+"F0.wireOp",EDGE,"E89.right"),sQuery(id+"F0.wireOp",EDGE,"E90.bottom"),sQuery(id+"F0.wireOp",EDGE,"E90.top"),sQuery(id+"F0.wireOp",EDGE,"E90.left"),sQuery(id+"F0.wireOp",EDGE,"E90.right"),sQuery(id+"F0.wireOp",EDGE,"E92.bottom"),sQuery(id+"F0.wireOp",EDGE,"E92.top"),sQuery(id+"F0.wireOp",EDGE,"E92.left"),sQuery(id+"F0.wireOp",EDGE,"E92.right"),sQuery(id+"F0.wireOp",EDGE,"E93.bottom"),sQuery(id+"F0.wireOp",EDGE,"E93.top"),sQuery(id+"F0.wireOp",EDGE,"E93.left"),sQuery(id+"F0.wireOp",EDGE,"E93.right")])],"isStart":false});
            var sketch = newSketch(context, id + "F2", { "sketchPlane" : qUnion([Q0])});
            skLineSegment(sketch, "E94.bottom", {"start": v(51.58, 19) * mm, "end": v(57.08, 19) * mm});
            skLineSegment(sketch, "E94.top", {"start": v(51.58, 11) * mm, "end": v(57.08, 11) * mm});
            skLineSegment(sketch, "E94.left", {"start": v(51.58, 19) * mm, "end": v(51.58, 11) * mm});
            skLineSegment(sketch, "E94.right", {"start": v(57.08, 19) * mm, "end": v(57.08, 11) * mm});
            skLineSegment(sketch, "E95.bottom", {"start": v(51.33, 18.92) * mm, "end": v(50.08, 18.92) * mm});
            skLineSegment(sketch, "E95.top", {"start": v(51.33, 18.42) * mm, "end": v(50.08, 18.42) * mm});
            skLineSegment(sketch, "E95.left", {"start": v(51.33, 18.92) * mm, "end": v(51.33, 18.42) * mm});
            skLineSegment(sketch, "E95.right", {"start": v(50.08, 18.92) * mm, "end": v(50.08, 18.42) * mm});
            skLineSegment(sketch, "E96", {"start": v(54.33, 19) * mm, "end": v(54.33, 11) * mm, "construction": true});
            skLineSegment(sketch, "E97", {"start": v(50.08, 18.67) * mm, "end": v(54.33, 18.67) * mm, "construction": true});
            skLineSegment(sketch, "E98.1.0.0", {"start": v(50.08, 18.25) * mm, "end": v(50.08, 17.75) * mm});
            skLineSegment(sketch, "E98.1.0.1", {"start": v(51.33, 18.25) * mm, "end": v(50.08, 18.25) * mm});
            skLineSegment(sketch, "E98.1.0.2", {"start": v(51.33, 18.25) * mm, "end": v(51.33, 17.75) * mm});
            skLineSegment(sketch, "E98.1.0.3", {"start": v(51.33, 17.75) * mm, "end": v(50.08, 17.75) * mm});
            skLineSegment(sketch, "E98.2.0.0", {"start": v(50.08, 17.58) * mm, "end": v(50.08, 17.08) * mm});
            skLineSegment(sketch, "E98.2.0.1", {"start": v(51.33, 17.58) * mm, "end": v(50.08, 17.58) * mm});
            skLineSegment(sketch, "E98.2.0.2", {"start": v(51.33, 17.58) * mm, "end": v(51.33, 17.08) * mm});
            skLineSegment(sketch, "E98.2.0.3", {"start": v(51.33, 17.08) * mm, "end": v(50.08, 17.08) * mm});
            skLineSegment(sketch, "E98.3.0.0", {"start": v(50.08, 16.92) * mm, "end": v(50.08, 16.42) * mm});
            skLineSegment(sketch, "E98.3.0.1", {"start": v(51.33, 16.92) * mm, "end": v(50.08, 16.92) * mm});
            skLineSegment(sketch, "E98.3.0.2", {"start": v(51.33, 16.92) * mm, "end": v(51.33, 16.42) * mm});
            skLineSegment(sketch, "E98.3.0.3", {"start": v(51.33, 16.42) * mm, "end": v(50.08, 16.42) * mm});
            skLineSegment(sketch, "E98.4.0.0", {"start": v(50.08, 16.25) * mm, "end": v(50.08, 15.75) * mm});
            skLineSegment(sketch, "E98.4.0.1", {"start": v(51.33, 16.25) * mm, "end": v(50.08, 16.25) * mm});
            skLineSegment(sketch, "E98.4.0.2", {"start": v(51.33, 16.25) * mm, "end": v(51.33, 15.75) * mm});
            skLineSegment(sketch, "E98.4.0.3", {"start": v(51.33, 15.75) * mm, "end": v(50.08, 15.75) * mm});
            skLineSegment(sketch, "E98.5.0.0", {"start": v(50.08, 15.58) * mm, "end": v(50.08, 15.08) * mm});
            skLineSegment(sketch, "E98.5.0.1", {"start": v(51.33, 15.58) * mm, "end": v(50.08, 15.58) * mm});
            skLineSegment(sketch, "E98.5.0.2", {"start": v(51.33, 15.58) * mm, "end": v(51.33, 15.08) * mm});
            skLineSegment(sketch, "E98.5.0.3", {"start": v(51.33, 15.08) * mm, "end": v(50.08, 15.08) * mm});
            skLineSegment(sketch, "E98.6.0.0", {"start": v(50.08, 14.92) * mm, "end": v(50.08, 14.42) * mm});
            skLineSegment(sketch, "E98.6.0.1", {"start": v(51.33, 14.92) * mm, "end": v(50.08, 14.92) * mm});
            skLineSegment(sketch, "E98.6.0.2", {"start": v(51.33, 14.92) * mm, "end": v(51.33, 14.42) * mm});
            skLineSegment(sketch, "E98.6.0.3", {"start": v(51.33, 14.42) * mm, "end": v(50.08, 14.42) * mm});
            skLineSegment(sketch, "E98.7.0.0", {"start": v(50.08, 14.25) * mm, "end": v(50.08, 13.75) * mm});
            skLineSegment(sketch, "E98.7.0.1", {"start": v(51.33, 14.25) * mm, "end": v(50.08, 14.25) * mm});
            skLineSegment(sketch, "E98.7.0.2", {"start": v(51.33, 14.25) * mm, "end": v(51.33, 13.75) * mm});
            skLineSegment(sketch, "E98.7.0.3", {"start": v(51.33, 13.75) * mm, "end": v(50.08, 13.75) * mm});
            skLineSegment(sketch, "E98.8.0.0", {"start": v(50.08, 13.58) * mm, "end": v(50.08, 13.08) * mm});
            skLineSegment(sketch, "E98.8.0.1", {"start": v(51.33, 13.58) * mm, "end": v(50.08, 13.58) * mm});
            skLineSegment(sketch, "E98.8.0.2", {"start": v(51.33, 13.58) * mm, "end": v(51.33, 13.08) * mm});
            skLineSegment(sketch, "E98.8.0.3", {"start": v(51.33, 13.08) * mm, "end": v(50.08, 13.08) * mm});
            skLineSegment(sketch, "E98.9.0.0", {"start": v(50.08, 12.92) * mm, "end": v(50.08, 12.42) * mm});
            skLineSegment(sketch, "E98.9.0.1", {"start": v(51.33, 12.92) * mm, "end": v(50.08, 12.92) * mm});
            skLineSegment(sketch, "E98.9.0.2", {"start": v(51.33, 12.92) * mm, "end": v(51.33, 12.42) * mm});
            skLineSegment(sketch, "E98.9.0.3", {"start": v(51.33, 12.42) * mm, "end": v(50.08, 12.42) * mm});
            skLineSegment(sketch, "E98.10.0.0", {"start": v(50.08, 12.25) * mm, "end": v(50.08, 11.75) * mm});
            skLineSegment(sketch, "E98.10.0.1", {"start": v(51.33, 12.25) * mm, "end": v(50.08, 12.25) * mm});
            skLineSegment(sketch, "E98.10.0.2", {"start": v(51.33, 12.25) * mm, "end": v(51.33, 11.75) * mm});
            skLineSegment(sketch, "E98.10.0.3", {"start": v(51.33, 11.75) * mm, "end": v(50.08, 11.75) * mm});
            skLineSegment(sketch, "E98.11.0.0", {"start": v(50.08, 11.58) * mm, "end": v(50.08, 11.08) * mm});
            skLineSegment(sketch, "E98.11.0.1", {"start": v(51.33, 11.58) * mm, "end": v(50.08, 11.58) * mm});
            skLineSegment(sketch, "E98.11.0.2", {"start": v(51.33, 11.58) * mm, "end": v(51.33, 11.08) * mm});
            skLineSegment(sketch, "E98.11.0.3", {"start": v(51.33, 11.08) * mm, "end": v(50.08, 11.08) * mm});
            skLineSegment(sketch, "E98.direction1", {"start": v(50.08, 18.42) * mm, "end": v(50.08, 17.75) * mm, "construction": true});
            skLineSegment(sketch, "E99.MirrorCS", {"start": v(58.58, 18.25) * mm, "end": v(58.58, 17.75) * mm});
            skLineSegment(sketch, "E100.MirrorCS", {"start": v(57.33, 12.92) * mm, "end": v(57.33, 12.42) * mm});
            skLineSegment(sketch, "E101.MirrorCS", {"start": v(58.58, 12.25) * mm, "end": v(58.58, 11.75) * mm});
            skLineSegment(sketch, "E102.MirrorCS", {"start": v(57.33, 12.25) * mm, "end": v(57.33, 11.75) * mm});
            skLineSegment(sketch, "E103.MirrorCS", {"start": v(57.33, 17.58) * mm, "end": v(57.33, 17.08) * mm});
            skLineSegment(sketch, "E104.MirrorCS", {"start": v(58.58, 16.92) * mm, "end": v(58.58, 16.42) * mm});
            skLineSegment(sketch, "E105.MirrorCS", {"start": v(58.58, 11.58) * mm, "end": v(58.58, 11.08) * mm});
            skLineSegment(sketch, "E106.MirrorCS", {"start": v(58.58, 18.42) * mm, "end": v(58.58, 17.75) * mm, "construction": true});
            skLineSegment(sketch, "E107.MirrorCS", {"start": v(57.33, 16.92) * mm, "end": v(57.33, 16.42) * mm});
            skLineSegment(sketch, "E108.MirrorCS", {"start": v(57.33, 18.25) * mm, "end": v(57.33, 17.75) * mm});
            skLineSegment(sketch, "E109.MirrorCS", {"start": v(58.58, 18.92) * mm, "end": v(58.58, 18.42) * mm});
            skLineSegment(sketch, "E110.MirrorCS", {"start": v(58.58, 12.92) * mm, "end": v(58.58, 12.42) * mm});
            skLineSegment(sketch, "E111.MirrorCS", {"start": v(58.58, 17.58) * mm, "end": v(58.58, 17.08) * mm});
            skLineSegment(sketch, "E112.MirrorCS", {"start": v(57.33, 11.58) * mm, "end": v(57.33, 11.08) * mm});
            skLineSegment(sketch, "E113.MirrorCS", {"start": v(57.33, 12.92) * mm, "end": v(58.58, 12.92) * mm});
            skLineSegment(sketch, "E114.MirrorCS", {"start": v(57.33, 15.58) * mm, "end": v(58.58, 15.58) * mm});
            skLineSegment(sketch, "E115.MirrorCS", {"start": v(57.33, 15.08) * mm, "end": v(58.58, 15.08) * mm});
            skLineSegment(sketch, "E116.MirrorCS", {"start": v(57.33, 12.42) * mm, "end": v(58.58, 12.42) * mm});
            skLineSegment(sketch, "E117.MirrorCS", {"start": v(57.33, 15.58) * mm, "end": v(57.33, 15.08) * mm});
            skLineSegment(sketch, "E118.MirrorCS", {"start": v(58.58, 14.92) * mm, "end": v(58.58, 14.42) * mm});
            skLineSegment(sketch, "E119.MirrorCS", {"start": v(57.33, 14.92) * mm, "end": v(58.58, 14.92) * mm});
            skLineSegment(sketch, "E120.MirrorCS", {"start": v(57.33, 12.25) * mm, "end": v(58.58, 12.25) * mm});
            skLineSegment(sketch, "E121.MirrorCS", {"start": v(57.33, 14.92) * mm, "end": v(57.33, 14.42) * mm});
            skLineSegment(sketch, "E122.MirrorCS", {"start": v(57.33, 14.42) * mm, "end": v(58.58, 14.42) * mm});
            skLineSegment(sketch, "E123.MirrorCS", {"start": v(57.33, 17.08) * mm, "end": v(58.58, 17.08) * mm});
            skLineSegment(sketch, "E124.MirrorCS", {"start": v(57.33, 11.75) * mm, "end": v(58.58, 11.75) * mm});
            skLineSegment(sketch, "E125.MirrorCS", {"start": v(58.58, 14.25) * mm, "end": v(58.58, 13.75) * mm});
            skLineSegment(sketch, "E126.MirrorCS", {"start": v(57.33, 14.25) * mm, "end": v(58.58, 14.25) * mm});
            skLineSegment(sketch, "E127.MirrorCS", {"start": v(57.33, 16.25) * mm, "end": v(58.58, 16.25) * mm});
            skLineSegment(sketch, "E128.MirrorCS", {"start": v(57.33, 13.58) * mm, "end": v(58.58, 13.58) * mm});
            skLineSegment(sketch, "E129.MirrorCS", {"start": v(57.33, 18.42) * mm, "end": v(58.58, 18.42) * mm});
            skLineSegment(sketch, "E130.MirrorCS", {"start": v(57.33, 18.92) * mm, "end": v(58.58, 18.92) * mm});
            skLineSegment(sketch, "E131.MirrorCS", {"start": v(57.33, 17.58) * mm, "end": v(58.58, 17.58) * mm});
            skLineSegment(sketch, "E132.MirrorCS", {"start": v(57.33, 14.25) * mm, "end": v(57.33, 13.75) * mm});
            skLineSegment(sketch, "E133.MirrorCS", {"start": v(58.58, 15.58) * mm, "end": v(58.58, 15.08) * mm});
            skLineSegment(sketch, "E134.MirrorCS", {"start": v(57.33, 11.08) * mm, "end": v(58.58, 11.08) * mm});
            skLineSegment(sketch, "E135.MirrorCS", {"start": v(57.33, 16.92) * mm, "end": v(58.58, 16.92) * mm});
            skLineSegment(sketch, "E136.MirrorCS", {"start": v(57.33, 17.75) * mm, "end": v(58.58, 17.75) * mm});
            skLineSegment(sketch, "E137.MirrorCS", {"start": v(57.33, 13.08) * mm, "end": v(58.58, 13.08) * mm});
            skLineSegment(sketch, "E138.MirrorCS", {"start": v(57.33, 18.25) * mm, "end": v(58.58, 18.25) * mm});
            skLineSegment(sketch, "E139.MirrorCS", {"start": v(57.33, 15.75) * mm, "end": v(58.58, 15.75) * mm});
            skLineSegment(sketch, "E140.MirrorCS", {"start": v(57.33, 18.92) * mm, "end": v(57.33, 18.42) * mm});
            skLineSegment(sketch, "E141.MirrorCS", {"start": v(57.33, 16.42) * mm, "end": v(58.58, 16.42) * mm});
            skLineSegment(sketch, "E142.MirrorCS", {"start": v(57.33, 13.75) * mm, "end": v(58.58, 13.75) * mm});
            skLineSegment(sketch, "E143.MirrorCS", {"start": v(57.33, 11.58) * mm, "end": v(58.58, 11.58) * mm});
            skLineSegment(sketch, "E144.MirrorCS", {"start": v(57.33, 16.25) * mm, "end": v(57.33, 15.75) * mm});
            skLineSegment(sketch, "E145.MirrorCS", {"start": v(57.33, 13.58) * mm, "end": v(57.33, 13.08) * mm});
            skLineSegment(sketch, "E146.MirrorCS", {"start": v(58.58, 13.58) * mm, "end": v(58.58, 13.08) * mm});
            skLineSegment(sketch, "E147.MirrorCS", {"start": v(58.58, 16.25) * mm, "end": v(58.58, 15.75) * mm});
            skLineSegment(sketch, "E148.bottom", {"start": v(11, 27) * mm, "end": v(16.5, 27) * mm});
            skLineSegment(sketch, "E148.top", {"start": v(11, 19) * mm, "end": v(16.5, 19) * mm});
            skLineSegment(sketch, "E148.left", {"start": v(11, 27) * mm, "end": v(11, 19) * mm});
            skLineSegment(sketch, "E148.right", {"start": v(16.5, 27) * mm, "end": v(16.5, 19) * mm});
            skLineSegment(sketch, "E149", {"start": v(13.75, 27) * mm, "end": v(13.75, 19) * mm, "construction": true});
            skLineSegment(sketch, "E150.bottom", {"start": v(9.5, 26.92) * mm, "end": v(10.75, 26.92) * mm});
            skLineSegment(sketch, "E150.top", {"start": v(9.5, 26.42) * mm, "end": v(10.75, 26.42) * mm});
            skLineSegment(sketch, "E150.left", {"start": v(9.5, 26.92) * mm, "end": v(9.5, 26.42) * mm});
            skLineSegment(sketch, "E150.right", {"start": v(10.75, 26.92) * mm, "end": v(10.75, 26.42) * mm});
            skLineSegment(sketch, "E151", {"start": v(9.5, 26.67) * mm, "end": v(13.75, 26.67) * mm, "construction": true});
            skLineSegment(sketch, "E152.1.0.0", {"start": v(10.75, 26.25) * mm, "end": v(10.75, 25.75) * mm});
            skLineSegment(sketch, "E152.1.0.1", {"start": v(9.5, 26.25) * mm, "end": v(9.5, 25.75) * mm});
            skLineSegment(sketch, "E152.1.0.2", {"start": v(9.5, 25.75) * mm, "end": v(10.75, 25.75) * mm});
            skLineSegment(sketch, "E152.1.0.3", {"start": v(9.5, 26.25) * mm, "end": v(10.75, 26.25) * mm});
            skLineSegment(sketch, "E152.2.0.0", {"start": v(10.75, 25.58) * mm, "end": v(10.75, 25.08) * mm});
            skLineSegment(sketch, "E152.2.0.1", {"start": v(9.5, 25.58) * mm, "end": v(9.5, 25.08) * mm});
            skLineSegment(sketch, "E152.2.0.2", {"start": v(9.5, 25.08) * mm, "end": v(10.75, 25.08) * mm});
            skLineSegment(sketch, "E152.2.0.3", {"start": v(9.5, 25.58) * mm, "end": v(10.75, 25.58) * mm});
            skLineSegment(sketch, "E152.3.0.0", {"start": v(10.75, 24.92) * mm, "end": v(10.75, 24.42) * mm});
            skLineSegment(sketch, "E152.3.0.1", {"start": v(9.5, 24.92) * mm, "end": v(9.5, 24.42) * mm});
            skLineSegment(sketch, "E152.3.0.2", {"start": v(9.5, 24.42) * mm, "end": v(10.75, 24.42) * mm});
            skLineSegment(sketch, "E152.3.0.3", {"start": v(9.5, 24.92) * mm, "end": v(10.75, 24.92) * mm});
            skLineSegment(sketch, "E152.4.0.0", {"start": v(10.75, 24.25) * mm, "end": v(10.75, 23.75) * mm});
            skLineSegment(sketch, "E152.4.0.1", {"start": v(9.5, 24.25) * mm, "end": v(9.5, 23.75) * mm});
            skLineSegment(sketch, "E152.4.0.2", {"start": v(9.5, 23.75) * mm, "end": v(10.75, 23.75) * mm});
            skLineSegment(sketch, "E152.4.0.3", {"start": v(9.5, 24.25) * mm, "end": v(10.75, 24.25) * mm});
            skLineSegment(sketch, "E152.5.0.0", {"start": v(10.75, 23.58) * mm, "end": v(10.75, 23.08) * mm});
            skLineSegment(sketch, "E152.5.0.1", {"start": v(9.5, 23.58) * mm, "end": v(9.5, 23.08) * mm});
            skLineSegment(sketch, "E152.5.0.2", {"start": v(9.5, 23.08) * mm, "end": v(10.75, 23.08) * mm});
            skLineSegment(sketch, "E152.5.0.3", {"start": v(9.5, 23.58) * mm, "end": v(10.75, 23.58) * mm});
            skLineSegment(sketch, "E152.6.0.0", {"start": v(10.75, 22.92) * mm, "end": v(10.75, 22.42) * mm});
            skLineSegment(sketch, "E152.6.0.1", {"start": v(9.5, 22.92) * mm, "end": v(9.5, 22.42) * mm});
            skLineSegment(sketch, "E152.6.0.2", {"start": v(9.5, 22.42) * mm, "end": v(10.75, 22.42) * mm});
            skLineSegment(sketch, "E152.6.0.3", {"start": v(9.5, 22.92) * mm, "end": v(10.75, 22.92) * mm});
            skLineSegment(sketch, "E152.7.0.0", {"start": v(10.75, 22.25) * mm, "end": v(10.75, 21.75) * mm});
            skLineSegment(sketch, "E152.7.0.1", {"start": v(9.5, 22.25) * mm, "end": v(9.5, 21.75) * mm});
            skLineSegment(sketch, "E152.7.0.2", {"start": v(9.5, 21.75) * mm, "end": v(10.75, 21.75) * mm});
            skLineSegment(sketch, "E152.7.0.3", {"start": v(9.5, 22.25) * mm, "end": v(10.75, 22.25) * mm});
            skLineSegment(sketch, "E152.8.0.0", {"start": v(10.75, 21.58) * mm, "end": v(10.75, 21.08) * mm});
            skLineSegment(sketch, "E152.8.0.1", {"start": v(9.5, 21.58) * mm, "end": v(9.5, 21.08) * mm});
            skLineSegment(sketch, "E152.8.0.2", {"start": v(9.5, 21.08) * mm, "end": v(10.75, 21.08) * mm});
            skLineSegment(sketch, "E152.8.0.3", {"start": v(9.5, 21.58) * mm, "end": v(10.75, 21.58) * mm});
            skLineSegment(sketch, "E152.9.0.0", {"start": v(10.75, 20.92) * mm, "end": v(10.75, 20.42) * mm});
            skLineSegment(sketch, "E152.9.0.1", {"start": v(9.5, 20.92) * mm, "end": v(9.5, 20.42) * mm});
            skLineSegment(sketch, "E152.9.0.2", {"start": v(9.5, 20.42) * mm, "end": v(10.75, 20.42) * mm});
            skLineSegment(sketch, "E152.9.0.3", {"start": v(9.5, 20.92) * mm, "end": v(10.75, 20.92) * mm});
            skLineSegment(sketch, "E152.10.0.0", {"start": v(10.75, 20.25) * mm, "end": v(10.75, 19.75) * mm});
            skLineSegment(sketch, "E152.10.0.1", {"start": v(9.5, 20.25) * mm, "end": v(9.5, 19.75) * mm});
            skLineSegment(sketch, "E152.10.0.2", {"start": v(9.5, 19.75) * mm, "end": v(10.75, 19.75) * mm});
            skLineSegment(sketch, "E152.10.0.3", {"start": v(9.5, 20.25) * mm, "end": v(10.75, 20.25) * mm});
            skLineSegment(sketch, "E152.11.0.0", {"start": v(10.75, 19.58) * mm, "end": v(10.75, 19.08) * mm});
            skLineSegment(sketch, "E152.11.0.1", {"start": v(9.5, 19.58) * mm, "end": v(9.5, 19.08) * mm});
            skLineSegment(sketch, "E152.11.0.2", {"start": v(9.5, 19.08) * mm, "end": v(10.75, 19.08) * mm});
            skLineSegment(sketch, "E152.11.0.3", {"start": v(9.5, 19.58) * mm, "end": v(10.75, 19.58) * mm});
            skLineSegment(sketch, "E152.direction1", {"start": v(9.5, 26.42) * mm, "end": v(9.5, 25.75) * mm, "construction": true});
            skLineSegment(sketch, "E153.MirrorCS", {"start": v(18, 26.92) * mm, "end": v(18, 26.42) * mm});
            skLineSegment(sketch, "E154.MirrorCS", {"start": v(18, 26.25) * mm, "end": v(18, 25.75) * mm});
            skLineSegment(sketch, "E155.MirrorCS", {"start": v(18, 21.08) * mm, "end": v(16.75, 21.08) * mm});
            skLineSegment(sketch, "E156.MirrorCS", {"start": v(18, 23.75) * mm, "end": v(16.75, 23.75) * mm});
            skLineSegment(sketch, "E157.MirrorCS", {"start": v(16.75, 26.92) * mm, "end": v(16.75, 26.42) * mm});
            skLineSegment(sketch, "E158.MirrorCS", {"start": v(18, 21.58) * mm, "end": v(18, 21.08) * mm});
            skLineSegment(sketch, "E159.MirrorCS", {"start": v(18, 24.42) * mm, "end": v(16.75, 24.42) * mm});
            skLineSegment(sketch, "E160.MirrorCS", {"start": v(18, 24.25) * mm, "end": v(18, 23.75) * mm});
            skLineSegment(sketch, "E161.MirrorCS", {"start": v(18, 26.92) * mm, "end": v(16.75, 26.92) * mm});
            skLineSegment(sketch, "E162.MirrorCS", {"start": v(18, 26.42) * mm, "end": v(18, 25.75) * mm, "construction": true});
            skLineSegment(sketch, "E163.MirrorCS", {"start": v(16.75, 21.58) * mm, "end": v(16.75, 21.08) * mm});
            skLineSegment(sketch, "E164.MirrorCS", {"start": v(16.75, 24.25) * mm, "end": v(16.75, 23.75) * mm});
            skLineSegment(sketch, "E165.MirrorCS", {"start": v(18, 26.42) * mm, "end": v(16.75, 26.42) * mm});
            skLineSegment(sketch, "E166.MirrorCS", {"start": v(18, 19.58) * mm, "end": v(16.75, 19.58) * mm});
            skLineSegment(sketch, "E167.MirrorCS", {"start": v(18, 24.92) * mm, "end": v(16.75, 24.92) * mm});
            skLineSegment(sketch, "E168.MirrorCS", {"start": v(18, 22.25) * mm, "end": v(16.75, 22.25) * mm});
            skLineSegment(sketch, "E169.MirrorCS", {"start": v(18, 21.75) * mm, "end": v(16.75, 21.75) * mm});
            skLineSegment(sketch, "E170.MirrorCS", {"start": v(18, 19.08) * mm, "end": v(16.75, 19.08) * mm});
            skLineSegment(sketch, "E171.MirrorCS", {"start": v(16.75, 24.92) * mm, "end": v(16.75, 24.42) * mm});
            skLineSegment(sketch, "E172.MirrorCS", {"start": v(16.75, 22.25) * mm, "end": v(16.75, 21.75) * mm});
            skLineSegment(sketch, "E173.MirrorCS", {"start": v(16.75, 19.58) * mm, "end": v(16.75, 19.08) * mm});
            skLineSegment(sketch, "E174.MirrorCS", {"start": v(18, 25.58) * mm, "end": v(16.75, 25.58) * mm});
            skLineSegment(sketch, "E175.MirrorCS", {"start": v(18, 22.92) * mm, "end": v(16.75, 22.92) * mm});
            skLineSegment(sketch, "E176.MirrorCS", {"start": v(18, 20.25) * mm, "end": v(16.75, 20.25) * mm});
            skLineSegment(sketch, "E177.MirrorCS", {"start": v(18, 19.58) * mm, "end": v(18, 19.08) * mm});
            skLineSegment(sketch, "E178.MirrorCS", {"start": v(18, 22.25) * mm, "end": v(18, 21.75) * mm});
            skLineSegment(sketch, "E179.MirrorCS", {"start": v(18, 24.92) * mm, "end": v(18, 24.42) * mm});
            skLineSegment(sketch, "E180.MirrorCS", {"start": v(18, 21.58) * mm, "end": v(16.75, 21.58) * mm});
            skLineSegment(sketch, "E181.MirrorCS", {"start": v(18, 24.25) * mm, "end": v(16.75, 24.25) * mm});
            skLineSegment(sketch, "E182.MirrorCS", {"start": v(16.75, 23.58) * mm, "end": v(16.75, 23.08) * mm});
            skLineSegment(sketch, "E183.MirrorCS", {"start": v(16.75, 26.25) * mm, "end": v(16.75, 25.75) * mm});
            skLineSegment(sketch, "E184.MirrorCS", {"start": v(16.75, 20.92) * mm, "end": v(16.75, 20.42) * mm});
            skLineSegment(sketch, "E185.MirrorCS", {"start": v(18, 23.58) * mm, "end": v(18, 23.08) * mm});
            skLineSegment(sketch, "E186.MirrorCS", {"start": v(18, 20.92) * mm, "end": v(18, 20.42) * mm});
            skLineSegment(sketch, "E187.MirrorCS", {"start": v(18, 23.08) * mm, "end": v(16.75, 23.08) * mm});
            skLineSegment(sketch, "E188.MirrorCS", {"start": v(18, 25.75) * mm, "end": v(16.75, 25.75) * mm});
            skLineSegment(sketch, "E189.MirrorCS", {"start": v(18, 20.42) * mm, "end": v(16.75, 20.42) * mm});
            skLineSegment(sketch, "E190.MirrorCS", {"start": v(16.75, 20.25) * mm, "end": v(16.75, 19.75) * mm});
            skLineSegment(sketch, "E191.MirrorCS", {"start": v(16.75, 22.92) * mm, "end": v(16.75, 22.42) * mm});
            skLineSegment(sketch, "E192.MirrorCS", {"start": v(16.75, 25.58) * mm, "end": v(16.75, 25.08) * mm});
            skLineSegment(sketch, "E193.MirrorCS", {"start": v(18, 25.58) * mm, "end": v(18, 25.08) * mm});
            skLineSegment(sketch, "E194.MirrorCS", {"start": v(18, 22.92) * mm, "end": v(18, 22.42) * mm});
            skLineSegment(sketch, "E195.MirrorCS", {"start": v(18, 20.25) * mm, "end": v(18, 19.75) * mm});
            skLineSegment(sketch, "E196.MirrorCS", {"start": v(18, 26.25) * mm, "end": v(16.75, 26.25) * mm});
            skLineSegment(sketch, "E197.MirrorCS", {"start": v(18, 23.58) * mm, "end": v(16.75, 23.58) * mm});
            skLineSegment(sketch, "E198.MirrorCS", {"start": v(18, 22.42) * mm, "end": v(16.75, 22.42) * mm});
            skLineSegment(sketch, "E199.MirrorCS", {"start": v(18, 19.75) * mm, "end": v(16.75, 19.75) * mm});
            skLineSegment(sketch, "E200.MirrorCS", {"start": v(18, 25.08) * mm, "end": v(16.75, 25.08) * mm});
            skLineSegment(sketch, "E201.MirrorCS", {"start": v(18, 20.92) * mm, "end": v(16.75, 20.92) * mm});
            skLineSegment(sketch, "E202.bottom", {"start": v(32.58, 27.44) * mm, "end": v(36.88, 27.44) * mm});
            skLineSegment(sketch, "E202.top", {"start": v(32.58, 17.64) * mm, "end": v(36.88, 17.64) * mm});
            skLineSegment(sketch, "E202.left", {"start": v(32.58, 27.44) * mm, "end": v(32.58, 17.64) * mm});
            skLineSegment(sketch, "E202.right", {"start": v(36.88, 27.44) * mm, "end": v(36.88, 17.64) * mm});
            skLineSegment(sketch, "E203.bottom", {"start": v(31.08, 27.12) * mm, "end": v(32.33, 27.12) * mm});
            skLineSegment(sketch, "E203.top", {"start": v(31.08, 26.62) * mm, "end": v(32.33, 26.62) * mm});
            skLineSegment(sketch, "E203.left", {"start": v(31.08, 27.12) * mm, "end": v(31.08, 26.62) * mm});
            skLineSegment(sketch, "E203.right", {"start": v(32.33, 27.12) * mm, "end": v(32.33, 26.62) * mm});
            skLineSegment(sketch, "E204", {"start": v(34.73, 27.44) * mm, "end": v(34.73, 17.64) * mm, "construction": true});
            skLineSegment(sketch, "E205", {"start": v(31.08, 26.87) * mm, "end": v(34.73, 26.87) * mm, "construction": true});
            skLineSegment(sketch, "E206.1.0.0", {"start": v(32.33, 26.46) * mm, "end": v(32.33, 25.96) * mm});
            skLineSegment(sketch, "E206.1.0.1", {"start": v(31.08, 26.46) * mm, "end": v(31.08, 25.96) * mm});
            skLineSegment(sketch, "E206.1.0.2", {"start": v(31.08, 25.96) * mm, "end": v(32.33, 25.96) * mm});
            skLineSegment(sketch, "E206.1.0.3", {"start": v(31.08, 26.46) * mm, "end": v(32.33, 26.46) * mm});
            skLineSegment(sketch, "E206.2.0.0", {"start": v(32.33, 25.8) * mm, "end": v(32.33, 25.3) * mm});
            skLineSegment(sketch, "E206.2.0.1", {"start": v(31.08, 25.8) * mm, "end": v(31.08, 25.3) * mm});
            skLineSegment(sketch, "E206.2.0.2", {"start": v(31.08, 25.3) * mm, "end": v(32.33, 25.3) * mm});
            skLineSegment(sketch, "E206.2.0.3", {"start": v(31.08, 25.8) * mm, "end": v(32.33, 25.8) * mm});
            skLineSegment(sketch, "E206.3.0.0", {"start": v(32.33, 25.12) * mm, "end": v(32.33, 24.62) * mm});
            skLineSegment(sketch, "E206.3.0.1", {"start": v(31.08, 25.12) * mm, "end": v(31.08, 24.62) * mm});
            skLineSegment(sketch, "E206.3.0.2", {"start": v(31.08, 24.62) * mm, "end": v(32.33, 24.62) * mm});
            skLineSegment(sketch, "E206.3.0.3", {"start": v(31.08, 25.12) * mm, "end": v(32.33, 25.12) * mm});
            skLineSegment(sketch, "E206.4.0.0", {"start": v(32.33, 24.46) * mm, "end": v(32.33, 23.96) * mm});
            skLineSegment(sketch, "E206.4.0.1", {"start": v(31.08, 24.46) * mm, "end": v(31.08, 23.96) * mm});
            skLineSegment(sketch, "E206.4.0.2", {"start": v(31.08, 23.96) * mm, "end": v(32.33, 23.96) * mm});
            skLineSegment(sketch, "E206.4.0.3", {"start": v(31.08, 24.46) * mm, "end": v(32.33, 24.46) * mm});
            skLineSegment(sketch, "E206.5.0.0", {"start": v(32.33, 23.8) * mm, "end": v(32.33, 23.3) * mm});
            skLineSegment(sketch, "E206.5.0.1", {"start": v(31.08, 23.8) * mm, "end": v(31.08, 23.3) * mm});
            skLineSegment(sketch, "E206.5.0.2", {"start": v(31.08, 23.3) * mm, "end": v(32.33, 23.3) * mm});
            skLineSegment(sketch, "E206.5.0.3", {"start": v(31.08, 23.8) * mm, "end": v(32.33, 23.8) * mm});
            skLineSegment(sketch, "E206.6.0.0", {"start": v(32.33, 23.12) * mm, "end": v(32.33, 22.62) * mm});
            skLineSegment(sketch, "E206.6.0.1", {"start": v(31.08, 23.12) * mm, "end": v(31.08, 22.62) * mm});
            skLineSegment(sketch, "E206.6.0.2", {"start": v(31.08, 22.62) * mm, "end": v(32.33, 22.62) * mm});
            skLineSegment(sketch, "E206.6.0.3", {"start": v(31.08, 23.12) * mm, "end": v(32.33, 23.12) * mm});
            skLineSegment(sketch, "E206.7.0.0", {"start": v(32.33, 22.46) * mm, "end": v(32.33, 21.96) * mm});
            skLineSegment(sketch, "E206.7.0.1", {"start": v(31.08, 22.46) * mm, "end": v(31.08, 21.96) * mm});
            skLineSegment(sketch, "E206.7.0.2", {"start": v(31.08, 21.96) * mm, "end": v(32.33, 21.96) * mm});
            skLineSegment(sketch, "E206.7.0.3", {"start": v(31.08, 22.46) * mm, "end": v(32.33, 22.46) * mm});
            skLineSegment(sketch, "E206.8.0.0", {"start": v(32.33, 21.8) * mm, "end": v(32.33, 21.3) * mm});
            skLineSegment(sketch, "E206.8.0.1", {"start": v(31.08, 21.8) * mm, "end": v(31.08, 21.3) * mm});
            skLineSegment(sketch, "E206.8.0.2", {"start": v(31.08, 21.3) * mm, "end": v(32.33, 21.3) * mm});
            skLineSegment(sketch, "E206.8.0.3", {"start": v(31.08, 21.8) * mm, "end": v(32.33, 21.8) * mm});
            skLineSegment(sketch, "E206.9.0.0", {"start": v(32.33, 21.12) * mm, "end": v(32.33, 20.62) * mm});
            skLineSegment(sketch, "E206.9.0.1", {"start": v(31.08, 21.12) * mm, "end": v(31.08, 20.62) * mm});
            skLineSegment(sketch, "E206.9.0.2", {"start": v(31.08, 20.62) * mm, "end": v(32.33, 20.62) * mm});
            skLineSegment(sketch, "E206.9.0.3", {"start": v(31.08, 21.12) * mm, "end": v(32.33, 21.12) * mm});
            skLineSegment(sketch, "E206.10.0.0", {"start": v(32.33, 20.46) * mm, "end": v(32.33, 19.96) * mm});
            skLineSegment(sketch, "E206.10.0.1", {"start": v(31.08, 20.46) * mm, "end": v(31.08, 19.96) * mm});
            skLineSegment(sketch, "E206.10.0.2", {"start": v(31.08, 19.96) * mm, "end": v(32.33, 19.96) * mm});
            skLineSegment(sketch, "E206.10.0.3", {"start": v(31.08, 20.46) * mm, "end": v(32.33, 20.46) * mm});
            skLineSegment(sketch, "E206.11.0.0", {"start": v(32.33, 19.8) * mm, "end": v(32.33, 19.3) * mm});
            skLineSegment(sketch, "E206.11.0.1", {"start": v(31.08, 19.8) * mm, "end": v(31.08, 19.3) * mm});
            skLineSegment(sketch, "E206.11.0.2", {"start": v(31.08, 19.3) * mm, "end": v(32.33, 19.3) * mm});
            skLineSegment(sketch, "E206.11.0.3", {"start": v(31.08, 19.8) * mm, "end": v(32.33, 19.8) * mm});
            skLineSegment(sketch, "E206.12.0.0", {"start": v(32.33, 19.12) * mm, "end": v(32.33, 18.62) * mm});
            skLineSegment(sketch, "E206.12.0.1", {"start": v(31.08, 19.12) * mm, "end": v(31.08, 18.62) * mm});
            skLineSegment(sketch, "E206.12.0.2", {"start": v(31.08, 18.62) * mm, "end": v(32.33, 18.62) * mm});
            skLineSegment(sketch, "E206.12.0.3", {"start": v(31.08, 19.12) * mm, "end": v(32.33, 19.12) * mm});
            skLineSegment(sketch, "E206.13.0.0", {"start": v(32.33, 18.46) * mm, "end": v(32.33, 17.96) * mm});
            skLineSegment(sketch, "E206.13.0.1", {"start": v(31.08, 18.46) * mm, "end": v(31.08, 17.96) * mm});
            skLineSegment(sketch, "E206.13.0.2", {"start": v(31.08, 17.96) * mm, "end": v(32.33, 17.96) * mm});
            skLineSegment(sketch, "E206.13.0.3", {"start": v(31.08, 18.46) * mm, "end": v(32.33, 18.46) * mm});
            skLineSegment(sketch, "E206.direction1", {"start": v(31.08, 26.62) * mm, "end": v(31.08, 25.96) * mm, "construction": true});
            skLineSegment(sketch, "E207", {"start": v(31.08, 18.2) * mm, "end": v(34.73, 18.2) * mm, "construction": true});
            skLineSegment(sketch, "E208", {"start": v(33.82, 18.2) * mm, "end": v(33.82, 17.64) * mm, "construction": true});
            skLineSegment(sketch, "E209", {"start": v(33.82, 26.87) * mm, "end": v(33.82, 27.44) * mm, "construction": true});
            skLineSegment(sketch, "E210.MirrorCS", {"start": v(38.38, 26.46) * mm, "end": v(38.38, 25.96) * mm});
            skLineSegment(sketch, "E211.MirrorCS", {"start": v(38.38, 18.46) * mm, "end": v(38.38, 17.96) * mm});
            skLineSegment(sketch, "E212.MirrorCS", {"start": v(38.38, 27.12) * mm, "end": v(38.38, 26.62) * mm});
            skLineSegment(sketch, "E213.MirrorCS", {"start": v(37.13, 25.8) * mm, "end": v(37.13, 25.3) * mm});
            skLineSegment(sketch, "E214.MirrorCS", {"start": v(37.13, 23.12) * mm, "end": v(37.13, 22.62) * mm});
            skLineSegment(sketch, "E215.MirrorCS", {"start": v(38.38, 20.62) * mm, "end": v(37.13, 20.62) * mm});
            skLineSegment(sketch, "E216.MirrorCS", {"start": v(38.38, 18.46) * mm, "end": v(37.13, 18.46) * mm});
            skLineSegment(sketch, "E217.MirrorCS", {"start": v(38.38, 20.46) * mm, "end": v(38.38, 19.96) * mm});
            skLineSegment(sketch, "E218.MirrorCS", {"start": v(38.38, 17.96) * mm, "end": v(37.13, 17.96) * mm});
            skLineSegment(sketch, "E219.MirrorCS", {"start": v(38.38, 26.46) * mm, "end": v(37.13, 26.46) * mm});
            skLineSegment(sketch, "E220.MirrorCS", {"start": v(38.38, 23.8) * mm, "end": v(37.13, 23.8) * mm});
            skLineSegment(sketch, "E221.MirrorCS", {"start": v(38.38, 26.62) * mm, "end": v(38.38, 25.96) * mm, "construction": true});
            skLineSegment(sketch, "E222.MirrorCS", {"start": v(38.38, 25.8) * mm, "end": v(38.38, 25.3) * mm});
            skLineSegment(sketch, "E223.MirrorCS", {"start": v(37.13, 20.46) * mm, "end": v(37.13, 19.96) * mm});
            skLineSegment(sketch, "E224.MirrorCS", {"start": v(38.38, 21.12) * mm, "end": v(37.13, 21.12) * mm});
            skLineSegment(sketch, "E225.MirrorCS", {"start": v(38.38, 23.12) * mm, "end": v(38.38, 22.62) * mm});
            skLineSegment(sketch, "E226.MirrorCS", {"start": v(38.38, 19.8) * mm, "end": v(38.38, 19.3) * mm});
            skLineSegment(sketch, "E227.MirrorCS", {"start": v(37.13, 25.12) * mm, "end": v(37.13, 24.62) * mm});
            skLineSegment(sketch, "E228.MirrorCS", {"start": v(38.38, 25.3) * mm, "end": v(37.13, 25.3) * mm});
            skLineSegment(sketch, "E229.MirrorCS", {"start": v(38.38, 23.3) * mm, "end": v(37.13, 23.3) * mm});
            skLineSegment(sketch, "E230.MirrorCS", {"start": v(38.38, 22.46) * mm, "end": v(38.38, 21.96) * mm});
            skLineSegment(sketch, "E231.MirrorCS", {"start": v(37.13, 19.8) * mm, "end": v(37.13, 19.3) * mm});
            skLineSegment(sketch, "E232.MirrorCS", {"start": v(38.38, 25.8) * mm, "end": v(37.13, 25.8) * mm});
            skLineSegment(sketch, "E233.MirrorCS", {"start": v(38.38, 20.46) * mm, "end": v(37.13, 20.46) * mm});
            skLineSegment(sketch, "E234.MirrorCS", {"start": v(38.38, 19.96) * mm, "end": v(37.13, 19.96) * mm});
            skLineSegment(sketch, "E235.MirrorCS", {"start": v(38.38, 22.62) * mm, "end": v(37.13, 22.62) * mm});
            skLineSegment(sketch, "E236.MirrorCS", {"start": v(38.38, 25.96) * mm, "end": v(37.13, 25.96) * mm});
            skLineSegment(sketch, "E237.MirrorCS", {"start": v(38.38, 25.12) * mm, "end": v(38.38, 24.62) * mm});
            skLineSegment(sketch, "E238.MirrorCS", {"start": v(38.38, 23.12) * mm, "end": v(37.13, 23.12) * mm});
            skLineSegment(sketch, "E239.MirrorCS", {"start": v(37.13, 22.46) * mm, "end": v(37.13, 21.96) * mm});
            skLineSegment(sketch, "E240.MirrorCS", {"start": v(37.13, 18.46) * mm, "end": v(37.13, 17.96) * mm});
            skLineSegment(sketch, "E241.MirrorCS", {"start": v(37.13, 21.12) * mm, "end": v(37.13, 20.62) * mm});
            skLineSegment(sketch, "E242.MirrorCS", {"start": v(37.13, 26.46) * mm, "end": v(37.13, 25.96) * mm});
            skLineSegment(sketch, "E243.MirrorCS", {"start": v(37.13, 23.8) * mm, "end": v(37.13, 23.3) * mm});
            skLineSegment(sketch, "E244.MirrorCS", {"start": v(38.38, 21.8) * mm, "end": v(37.13, 21.8) * mm});
            skLineSegment(sketch, "E245.MirrorCS", {"start": v(38.38, 19.12) * mm, "end": v(37.13, 19.12) * mm});
            skLineSegment(sketch, "E246.MirrorCS", {"start": v(38.38, 23.8) * mm, "end": v(38.38, 23.3) * mm});
            skLineSegment(sketch, "E247.MirrorCS", {"start": v(38.38, 21.12) * mm, "end": v(38.38, 20.62) * mm});
            skLineSegment(sketch, "E248.MirrorCS", {"start": v(38.38, 19.3) * mm, "end": v(37.13, 19.3) * mm});
            skLineSegment(sketch, "E249.MirrorCS", {"start": v(38.38, 21.96) * mm, "end": v(37.13, 21.96) * mm});
            skLineSegment(sketch, "E250.MirrorCS", {"start": v(38.38, 24.62) * mm, "end": v(37.13, 24.62) * mm});
            skLineSegment(sketch, "E251.MirrorCS", {"start": v(38.38, 27.12) * mm, "end": v(37.13, 27.12) * mm});
            skLineSegment(sketch, "E252.MirrorCS", {"start": v(38.38, 19.8) * mm, "end": v(37.13, 19.8) * mm});
            skLineSegment(sketch, "E253.MirrorCS", {"start": v(38.38, 22.46) * mm, "end": v(37.13, 22.46) * mm});
            skLineSegment(sketch, "E254.MirrorCS", {"start": v(38.38, 26.62) * mm, "end": v(37.13, 26.62) * mm});
            skLineSegment(sketch, "E255.MirrorCS", {"start": v(38.38, 25.12) * mm, "end": v(37.13, 25.12) * mm});
            skLineSegment(sketch, "E256.MirrorCS", {"start": v(37.13, 24.46) * mm, "end": v(37.13, 23.96) * mm});
            skLineSegment(sketch, "E257.MirrorCS", {"start": v(37.13, 19.12) * mm, "end": v(37.13, 18.62) * mm});
            skLineSegment(sketch, "E258.MirrorCS", {"start": v(37.13, 21.8) * mm, "end": v(37.13, 21.3) * mm});
            skLineSegment(sketch, "E259.MirrorCS", {"start": v(38.38, 21.3) * mm, "end": v(37.13, 21.3) * mm});
            skLineSegment(sketch, "E260.MirrorCS", {"start": v(38.38, 18.62) * mm, "end": v(37.13, 18.62) * mm});
            skLineSegment(sketch, "E261.MirrorCS", {"start": v(38.38, 23.96) * mm, "end": v(37.13, 23.96) * mm});
            skLineSegment(sketch, "E262.MirrorCS", {"start": v(38.38, 19.12) * mm, "end": v(38.38, 18.62) * mm});
            skLineSegment(sketch, "E263.MirrorCS", {"start": v(38.38, 21.8) * mm, "end": v(38.38, 21.3) * mm});
            skLineSegment(sketch, "E264.MirrorCS", {"start": v(38.38, 24.46) * mm, "end": v(38.38, 23.96) * mm});
            skLineSegment(sketch, "E265.MirrorCS", {"start": v(37.13, 27.12) * mm, "end": v(37.13, 26.62) * mm});
            skLineSegment(sketch, "E266.MirrorCS", {"start": v(38.38, 24.46) * mm, "end": v(37.13, 24.46) * mm});
            skSolve(sketch);
        }
        {
            var Q0;
            Q0 = qSketchRegion(id + "F2", true);
            extrude(context, id + "F3", {"entities" : qUnion([Q0]), "operationType" : NewBodyOperationType.REMOVE, "oppositeDirection" : true, "depth" : 0.25 * mm});
        }
        {
            var Q0;
            Q0=makeQuery(id+"F1.opExtrude","CAP_FACE",FACE,{"disambiguationData":[OSD([sQuery(id+"F0.wireOp",EDGE,"E0.bottom"),sQuery(id+"F0.wireOp",EDGE,"E0.top"),sQuery(id+"F0.wireOp",EDGE,"E0.left"),sQuery(id+"F0.wireOp",EDGE,"E0.right"),sQuery(id+"F0.wireOp",EDGE,"E1"),sQuery(id+"F0.wireOp",EDGE,"E2"),sQuery(id+"F0.wireOp",EDGE,"E3"),sQuery(id+"F0.wireOp",EDGE,"E4.trimOffspring"),sQuery(id+"F0.wireOp",EDGE,"E5"),sQuery(id+"F0.wireOp",EDGE,"E6"),sQuery(id+"F0.wireOp",EDGE,"E7"),sQuery(id+"F0.wireOp",EDGE,"E9"),sQuery(id+"F0.wireOp",EDGE,"E10.1.0.0"),sQuery(id+"F0.wireOp",EDGE,"E10.2.0.0"),sQuery(id+"F0.wireOp",EDGE,"E10.3.0.0"),sQuery(id+"F0.wireOp",EDGE,"E10.4.0.0"),sQuery(id+"F0.wireOp",EDGE,"E10.5.0.0"),sQuery(id+"F0.wireOp",EDGE,"E10.6.0.0"),sQuery(id+"F0.wireOp",EDGE,"E10.7.0.0"),sQuery(id+"F0.wireOp",EDGE,"E11"),sQuery(id+"F0.wireOp",EDGE,"E12.1.0.0"),sQuery(id+"F0.wireOp",EDGE,"E12.2.0.0"),sQuery(id+"F0.wireOp",EDGE,"E12.3.0.0"),sQuery(id+"F0.wireOp",EDGE,"E12.4.0.0"),sQuery(id+"F0.wireOp",EDGE,"E12.5.0.0"),sQuery(id+"F0.wireOp",EDGE,"E12.6.0.0"),sQuery(id+"F0.wireOp",EDGE,"E12.7.0.0"),sQuery(id+"F0.wireOp",EDGE,"E12.8.0.0"),sQuery(id+"F0.wireOp",EDGE,"E12.9.0.0"),sQuery(id+"F0.wireOp",EDGE,"E14"),sQuery(id+"F0.wireOp",EDGE,"E15.1.0.0"),sQuery(id+"F0.wireOp",EDGE,"E15.2.0.0"),sQuery(id+"F0.wireOp",EDGE,"E15.3.0.0"),sQuery(id+"F0.wireOp",EDGE,"E15.4.0.0"),sQuery(id+"F0.wireOp",EDGE,"E15.5.0.0"),sQuery(id+"F0.wireOp",EDGE,"E16"),sQuery(id+"F0.wireOp",EDGE,"E17.1.0.0"),sQuery(id+"F0.wireOp",EDGE,"E17.2.0.0"),sQuery(id+"F0.wireOp",EDGE,"E17.3.0.0"),sQuery(id+"F0.wireOp",EDGE,"E17.4.0.0"),sQuery(id+"F0.wireOp",EDGE,"E17.5.0.0"),sQuery(id+"F0.wireOp",EDGE,"E17.6.0.0"),sQuery(id+"F0.wireOp",EDGE,"E17.7.0.0"),sQuery(id+"F0.wireOp",EDGE,"E19.1.0.2"),sQuery(id+"F0.wireOp",EDGE,"E19.1.0.3"),sQuery(id+"F0.wireOp",EDGE,"E19.1.0.4"),sQuery(id+"F0.wireOp",EDGE,"E19.1.0.6"),sQuery(id+"F0.wireOp",EDGE,"E19.1.0.7"),sQuery(id+"F0.wireOp",EDGE,"E19.1.0.8"),sQuery(id+"F0.wireOp",EDGE,"E19.1.0.9"),sQuery(id+"F0.wireOp",EDGE,"E19.1.0.10"),sQuery(id+"F0.wireOp",EDGE,"E19.1.0.11"),sQuery(id+"F0.wireOp",EDGE,"E19.1.0.12"),sQuery(id+"F0.wireOp",EDGE,"E19.1.0.13"),sQuery(id+"F0.wireOp",EDGE,"E19.1.0.14"),sQuery(id+"F0.wireOp",EDGE,"E19.1.0.15"),sQuery(id+"F0.wireOp",EDGE,"E19.1.0.16"),sQuery(id+"F0.wireOp",EDGE,"E19.1.0.17"),sQuery(id+"F0.wireOp",EDGE,"E19.1.0.18"),sQuery(id+"F0.wireOp",EDGE,"E19.1.0.19"),sQuery(id+"F0.wireOp",EDGE,"E21.1.0.1"),sQuery(id+"F0.wireOp",EDGE,"E21.1.0.2"),sQuery(id+"F0.wireOp",EDGE,"E21.1.0.3"),sQuery(id+"F0.wireOp",EDGE,"E21.1.0.4"),sQuery(id+"F0.wireOp",EDGE,"E21.1.0.5"),sQuery(id+"F0.wireOp",EDGE,"E21.1.0.6"),sQuery(id+"F0.wireOp",EDGE,"E21.1.0.7"),sQuery(id+"F0.wireOp",EDGE,"E21.1.0.8"),sQuery(id+"F0.wireOp",EDGE,"E21.1.0.9"),sQuery(id+"F0.wireOp",EDGE,"E21.1.0.10"),sQuery(id+"F0.wireOp",EDGE,"E21.1.0.11"),sQuery(id+"F0.wireOp",EDGE,"E21.1.0.12"),sQuery(id+"F0.wireOp",EDGE,"E25"),sQuery(id+"F0.wireOp",EDGE,"E26"),sQuery(id+"F0.wireOp",EDGE,"E27"),sQuery(id+"F0.wireOp",EDGE,"E28"),sQuery(id+"F0.wireOp",EDGE,"E29"),sQuery(id+"F0.wireOp",EDGE,"E30"),sQuery(id+"F0.wireOp",EDGE,"E31.1.0.0"),sQuery(id+"F0.wireOp",EDGE,"E31.1.0.1"),sQuery(id+"F0.wireOp",EDGE,"E31.1.0.2"),sQuery(id+"F0.wireOp",EDGE,"E31.1.0.3"),sQuery(id+"F0.wireOp",EDGE,"E31.1.0.4"),sQuery(id+"F0.wireOp",EDGE,"E31.1.0.5"),sQuery(id+"F0.wireOp",EDGE,"E31.2.0.0"),sQuery(id+"F0.wireOp",EDGE,"E31.2.0.1"),sQuery(id+"F0.wireOp",EDGE,"E31.2.0.2"),sQuery(id+"F0.wireOp",EDGE,"E31.2.0.3"),sQuery(id+"F0.wireOp",EDGE,"E31.2.0.4"),sQuery(id+"F0.wireOp",EDGE,"E31.2.0.5"),sQuery(id+"F0.wireOp",EDGE,"E31.3.0.0"),sQuery(id+"F0.wireOp",EDGE,"E31.3.0.1"),sQuery(id+"F0.wireOp",EDGE,"E31.3.0.2"),sQuery(id+"F0.wireOp",EDGE,"E31.3.0.3"),sQuery(id+"F0.wireOp",EDGE,"E31.3.0.4"),sQuery(id+"F0.wireOp",EDGE,"E31.3.0.5"),sQuery(id+"F0.wireOp",EDGE,"E31.4.0.0"),sQuery(id+"F0.wireOp",EDGE,"E31.4.0.1"),sQuery(id+"F0.wireOp",EDGE,"E31.4.0.2"),sQuery(id+"F0.wireOp",EDGE,"E31.4.0.3"),sQuery(id+"F0.wireOp",EDGE,"E31.4.0.4"),sQuery(id+"F0.wireOp",EDGE,"E31.4.0.5"),sQuery(id+"F0.wireOp",EDGE,"E31.5.0.0"),sQuery(id+"F0.wireOp",EDGE,"E31.5.0.1"),sQuery(id+"F0.wireOp",EDGE,"E31.5.0.2"),sQuery(id+"F0.wireOp",EDGE,"E31.5.0.3"),sQuery(id+"F0.wireOp",EDGE,"E31.5.0.4"),sQuery(id+"F0.wireOp",EDGE,"E31.5.0.5"),sQuery(id+"F0.wireOp",EDGE,"E31.6.0.0"),sQuery(id+"F0.wireOp",EDGE,"E31.6.0.1"),sQuery(id+"F0.wireOp",EDGE,"E31.6.0.2"),sQuery(id+"F0.wireOp",EDGE,"E31.6.0.3"),sQuery(id+"F0.wireOp",EDGE,"E31.6.0.4"),sQuery(id+"F0.wireOp",EDGE,"E31.6.0.5"),sQuery(id+"F0.wireOp",EDGE,"E31.7.0.0"),sQuery(id+"F0.wireOp",EDGE,"E31.7.0.1"),sQuery(id+"F0.wireOp",EDGE,"E31.7.0.2"),sQuery(id+"F0.wireOp",EDGE,"E31.7.0.3"),sQuery(id+"F0.wireOp",EDGE,"E31.7.0.4"),sQuery(id+"F0.wireOp",EDGE,"E31.7.0.5"),sQuery(id+"F0.wireOp",EDGE,"E31.8.0.0"),sQuery(id+"F0.wireOp",EDGE,"E31.8.0.1"),sQuery(id+"F0.wireOp",EDGE,"E31.8.0.2"),sQuery(id+"F0.wireOp",EDGE,"E31.8.0.3"),sQuery(id+"F0.wireOp",EDGE,"E31.8.0.4"),sQuery(id+"F0.wireOp",EDGE,"E31.8.0.5"),sQuery(id+"F0.wireOp",EDGE,"E31.9.0.0"),sQuery(id+"F0.wireOp",EDGE,"E31.9.0.1"),sQuery(id+"F0.wireOp",EDGE,"E31.9.0.2"),sQuery(id+"F0.wireOp",EDGE,"E31.9.0.3"),sQuery(id+"F0.wireOp",EDGE,"E31.9.0.4"),sQuery(id+"F0.wireOp",EDGE,"E31.9.0.5"),sQuery(id+"F0.wireOp",EDGE,"E31.10.0.0"),sQuery(id+"F0.wireOp",EDGE,"E31.10.0.1"),sQuery(id+"F0.wireOp",EDGE,"E31.10.0.2"),sQuery(id+"F0.wireOp",EDGE,"E31.10.0.3"),sQuery(id+"F0.wireOp",EDGE,"E31.10.0.4"),sQuery(id+"F0.wireOp",EDGE,"E31.10.0.5"),sQuery(id+"F0.wireOp",EDGE,"E31.11.0.0"),sQuery(id+"F0.wireOp",EDGE,"E31.11.0.1"),sQuery(id+"F0.wireOp",EDGE,"E31.11.0.2"),sQuery(id+"F0.wireOp",EDGE,"E31.11.0.3"),sQuery(id+"F0.wireOp",EDGE,"E31.11.0.4"),sQuery(id+"F0.wireOp",EDGE,"E31.11.0.5"),sQuery(id+"F0.wireOp",EDGE,"E31.12.0.0"),sQuery(id+"F0.wireOp",EDGE,"E31.12.0.1"),sQuery(id+"F0.wireOp",EDGE,"E31.12.0.2"),sQuery(id+"F0.wireOp",EDGE,"E31.12.0.3"),sQuery(id+"F0.wireOp",EDGE,"E31.12.0.4"),sQuery(id+"F0.wireOp",EDGE,"E31.12.0.5"),sQuery(id+"F0.wireOp",EDGE,"E31.13.0.0"),sQuery(id+"F0.wireOp",EDGE,"E31.13.0.1"),sQuery(id+"F0.wireOp",EDGE,"E31.13.0.2"),sQuery(id+"F0.wireOp",EDGE,"E31.13.0.3"),sQuery(id+"F0.wireOp",EDGE,"E31.13.0.4"),sQuery(id+"F0.wireOp",EDGE,"E31.13.0.5"),sQuery(id+"F0.wireOp",EDGE,"E31.14.0.0"),sQuery(id+"F0.wireOp",EDGE,"E31.14.0.1"),sQuery(id+"F0.wireOp",EDGE,"E31.14.0.2"),sQuery(id+"F0.wireOp",EDGE,"E31.14.0.3"),sQuery(id+"F0.wireOp",EDGE,"E31.14.0.4"),sQuery(id+"F0.wireOp",EDGE,"E31.14.0.5"),sQuery(id+"F0.wireOp",EDGE,"E31.15.0.0"),sQuery(id+"F0.wireOp",EDGE,"E31.15.0.1"),sQuery(id+"F0.wireOp",EDGE,"E31.15.0.2"),sQuery(id+"F0.wireOp",EDGE,"E31.15.0.3"),sQuery(id+"F0.wireOp",EDGE,"E31.15.0.4"),sQuery(id+"F0.wireOp",EDGE,"E31.15.0.5"),sQuery(id+"F0.wireOp",EDGE,"E31.16.0.0"),sQuery(id+"F0.wireOp",EDGE,"E31.16.0.1"),sQuery(id+"F0.wireOp",EDGE,"E31.16.0.2"),sQuery(id+"F0.wireOp",EDGE,"E31.16.0.3"),sQuery(id+"F0.wireOp",EDGE,"E31.16.0.4"),sQuery(id+"F0.wireOp",EDGE,"E31.16.0.5"),sQuery(id+"F0.wireOp",EDGE,"E31.17.0.0"),sQuery(id+"F0.wireOp",EDGE,"E31.17.0.1"),sQuery(id+"F0.wireOp",EDGE,"E31.17.0.2"),sQuery(id+"F0.wireOp",EDGE,"E31.17.0.3"),sQuery(id+"F0.wireOp",EDGE,"E31.17.0.4"),sQuery(id+"F0.wireOp",EDGE,"E31.17.0.5"),sQuery(id+"F0.wireOp",EDGE,"E31.18.0.0"),sQuery(id+"F0.wireOp",EDGE,"E31.18.0.1"),sQuery(id+"F0.wireOp",EDGE,"E31.18.0.2"),sQuery(id+"F0.wireOp",EDGE,"E31.18.0.3"),sQuery(id+"F0.wireOp",EDGE,"E31.18.0.4"),sQuery(id+"F0.wireOp",EDGE,"E31.18.0.5"),sQuery(id+"F0.wireOp",EDGE,"E32"),sQuery(id+"F0.wireOp",EDGE,"E33"),sQuery(id+"F0.wireOp",EDGE,"E34"),sQuery(id+"F0.wireOp",EDGE,"E36"),sQuery(id+"F0.wireOp",EDGE,"E37"),sQuery(id+"F0.wireOp",EDGE,"E38"),sQuery(id+"F0.wireOp",EDGE,"E39"),sQuery(id+"F0.wireOp",EDGE,"E40"),sQuery(id+"F0.wireOp",EDGE,"E41"),sQuery(id+"F0.wireOp",EDGE,"E42"),sQuery(id+"F0.wireOp",EDGE,"E43"),sQuery(id+"F0.wireOp",EDGE,"E44"),sQuery(id+"F0.wireOp",EDGE,"E45.bottom"),sQuery(id+"F0.wireOp",EDGE,"E45.top"),sQuery(id+"F0.wireOp",EDGE,"E45.left"),sQuery(id+"F0.wireOp",EDGE,"E45.right"),sQuery(id+"F0.wireOp",EDGE,"E46.bottom"),sQuery(id+"F0.wireOp",EDGE,"E46.top"),sQuery(id+"F0.wireOp",EDGE,"E46.left"),sQuery(id+"F0.wireOp",EDGE,"E46.right"),sQuery(id+"F0.wireOp",EDGE,"E47.bottom"),sQuery(id+"F0.wireOp",EDGE,"E47.top"),sQuery(id+"F0.wireOp",EDGE,"E47.left"),sQuery(id+"F0.wireOp",EDGE,"E47.right"),sQuery(id+"F0.wireOp",EDGE,"E56"),sQuery(id+"F0.wireOp",EDGE,"E57"),sQuery(id+"F0.wireOp",EDGE,"E58"),sQuery(id+"F0.wireOp",EDGE,"E59"),sQuery(id+"F0.wireOp",EDGE,"E60"),sQuery(id+"F0.wireOp",EDGE,"E69"),sQuery(id+"F0.wireOp",EDGE,"E70"),sQuery(id+"F0.wireOp",EDGE,"E71"),sQuery(id+"F0.wireOp",EDGE,"E72"),sQuery(id+"F0.wireOp",EDGE,"E73"),sQuery(id+"F0.wireOp",EDGE,"E79"),sQuery(id+"F0.wireOp",EDGE,"E80"),sQuery(id+"F0.wireOp",EDGE,"E85.bottom"),sQuery(id+"F0.wireOp",EDGE,"E85.top"),sQuery(id+"F0.wireOp",EDGE,"E85.left"),sQuery(id+"F0.wireOp",EDGE,"E85.right"),sQuery(id+"F0.wireOp",EDGE,"E86.bottom"),sQuery(id+"F0.wireOp",EDGE,"E86.top"),sQuery(id+"F0.wireOp",EDGE,"E86.left"),sQuery(id+"F0.wireOp",EDGE,"E86.right"),sQuery(id+"F0.wireOp",EDGE,"E87.bottom"),sQuery(id+"F0.wireOp",EDGE,"E87.top"),sQuery(id+"F0.wireOp",EDGE,"E87.left"),sQuery(id+"F0.wireOp",EDGE,"E87.right"),sQuery(id+"F0.wireOp",EDGE,"E88.bottom"),sQuery(id+"F0.wireOp",EDGE,"E88.top"),sQuery(id+"F0.wireOp",EDGE,"E88.left"),sQuery(id+"F0.wireOp",EDGE,"E88.right"),sQuery(id+"F0.wireOp",EDGE,"E89.bottom"),sQuery(id+"F0.wireOp",EDGE,"E89.top"),sQuery(id+"F0.wireOp",EDGE,"E89.left"),sQuery(id+"F0.wireOp",EDGE,"E89.right"),sQuery(id+"F0.wireOp",EDGE,"E90.bottom"),sQuery(id+"F0.wireOp",EDGE,"E90.top"),sQuery(id+"F0.wireOp",EDGE,"E90.left"),sQuery(id+"F0.wireOp",EDGE,"E90.right"),sQuery(id+"F0.wireOp",EDGE,"E92.bottom"),sQuery(id+"F0.wireOp",EDGE,"E92.top"),sQuery(id+"F0.wireOp",EDGE,"E92.left"),sQuery(id+"F0.wireOp",EDGE,"E92.right"),sQuery(id+"F0.wireOp",EDGE,"E93.bottom"),sQuery(id+"F0.wireOp",EDGE,"E93.top"),sQuery(id+"F0.wireOp",EDGE,"E93.left"),sQuery(id+"F0.wireOp",EDGE,"E93.right")])],"isStart":false});
            var sketch = newSketch(context, id + "F4", { "sketchPlane" : qUnion([Q0])});
            skLineSegment(sketch, "E267.bottom", {"start": v(45.78, 24.4) * mm, "end": v(49.88, 24.4) * mm, "construction": true});
            skLineSegment(sketch, "E267.top", {"start": v(45.78, 19.1) * mm, "end": v(49.88, 19.1) * mm, "construction": true});
            skLineSegment(sketch, "E267.left", {"start": v(45.78, 24.4) * mm, "end": v(45.78, 19.1) * mm, "construction": true});
            skLineSegment(sketch, "E267.right", {"start": v(51.08, 23.2) * mm, "end": v(51.08, 20.3) * mm, "construction": true});
            skLineSegment(sketch, "E268.bottom", {"start": v(11.2, 18) * mm, "end": v(15.3, 18) * mm, "construction": true});
            skLineSegment(sketch, "E268.top", {"start": v(11.2, 12.7) * mm, "end": v(15.3, 12.7) * mm, "construction": true});
            skLineSegment(sketch, "E268.left", {"start": v(11.2, 18) * mm, "end": v(11.2, 12.7) * mm, "construction": true});
            skLineSegment(sketch, "E268.right", {"start": v(16.5, 16.8) * mm, "end": v(16.5, 13.9) * mm, "construction": true});
            skLineSegment(sketch, "E269.bottom", {"start": v(5.9, 44.64) * mm, "end": v(10, 44.64) * mm, "construction": true});
            skLineSegment(sketch, "E269.top", {"start": v(5.9, 39.34) * mm, "end": v(10, 39.34) * mm, "construction": true});
            skLineSegment(sketch, "E269.left", {"start": v(4.7, 43.44) * mm, "end": v(4.7, 40.54) * mm, "construction": true});
            skLineSegment(sketch, "E269.right", {"start": v(10, 44.64) * mm, "end": v(10, 39.34) * mm, "construction": true});
            skLineSegment(sketch, "E270", {"start": v(4.7, 43.44) * mm, "end": v(5.9, 44.64) * mm, "construction": true});
            skLineSegment(sketch, "E271", {"start": v(4.7, 40.54) * mm, "end": v(5.9, 39.34) * mm, "construction": true});
            skPoint(sketch, "E272.orphan", {"position": v(4.7, 44.64) * mm});
            skPoint(sketch, "E273.orphan", {"position": v(4.7, 39.34) * mm});
            skLineSegment(sketch, "E274", {"start": v(15.3, 18) * mm, "end": v(16.5, 16.8) * mm, "construction": true});
            skLineSegment(sketch, "E275", {"start": v(16.5, 13.9) * mm, "end": v(15.3, 12.7) * mm, "construction": true});
            skPoint(sketch, "E276.orphan", {"position": v(16.5, 18) * mm});
            skPoint(sketch, "E277.orphan", {"position": v(16.5, 12.7) * mm});
            skLineSegment(sketch, "E278", {"start": v(51.08, 20.3) * mm, "end": v(49.88, 19.1) * mm, "construction": true});
            skLineSegment(sketch, "E279", {"start": v(49.88, 24.4) * mm, "end": v(51.08, 23.2) * mm, "construction": true});
            skPoint(sketch, "E280.orphan", {"position": v(51.08, 24.4) * mm});
            skPoint(sketch, "E281.orphan", {"position": v(51.08, 19.1) * mm});
            skCircle(sketch, "E282", {"center": v(46.43, 21.75) * mm, "radius": 0.3 * mm});
            skCircle(sketch, "E283", {"center": v(50.43, 21.75) * mm, "radius": 0.3 * mm});
            skLineSegment(sketch, "E284", {"start": v(45.78, 21.75) * mm, "end": v(51.08, 21.75) * mm, "construction": true});
            skLineSegment(sketch, "E285", {"start": v(11.2, 15.35) * mm, "end": v(16.5, 15.35) * mm, "construction": true});
            skCircle(sketch, "E286", {"center": v(11.85, 15.35) * mm, "radius": 0.3 * mm});
            skCircle(sketch, "E287", {"center": v(15.85, 15.35) * mm, "radius": 0.3 * mm});
            skLineSegment(sketch, "E288", {"start": v(4.7, 42) * mm, "end": v(10, 42) * mm, "construction": true});
            skCircle(sketch, "E289", {"center": v(5.35, 42) * mm, "radius": 0.3 * mm});
            skCircle(sketch, "E290", {"center": v(9.35, 42) * mm, "radius": 0.3 * mm});
            skSolve(sketch);
        }
        {
            var Q0;
            Q0 = qSketchRegion(id + "F4", true);
            extrude(context, id + "F5", {"entities" : qUnion([Q0]), "operationType" : NewBodyOperationType.REMOVE, "oppositeDirection" : true, "depth" : 0.5 * mm});
        }
        {
            var Q0;
            Q0=makeQuery(id+"F1.opExtrude","CAP_FACE",FACE,{"disambiguationData":[OSD([sQuery(id+"F0.wireOp",EDGE,"E0.bottom"),sQuery(id+"F0.wireOp",EDGE,"E0.top"),sQuery(id+"F0.wireOp",EDGE,"E0.left"),sQuery(id+"F0.wireOp",EDGE,"E0.right"),sQuery(id+"F0.wireOp",EDGE,"E1"),sQuery(id+"F0.wireOp",EDGE,"E2"),sQuery(id+"F0.wireOp",EDGE,"E3"),sQuery(id+"F0.wireOp",EDGE,"E4.trimOffspring"),sQuery(id+"F0.wireOp",EDGE,"E5"),sQuery(id+"F0.wireOp",EDGE,"E6"),sQuery(id+"F0.wireOp",EDGE,"E7"),sQuery(id+"F0.wireOp",EDGE,"E9"),sQuery(id+"F0.wireOp",EDGE,"E10.1.0.0"),sQuery(id+"F0.wireOp",EDGE,"E10.2.0.0"),sQuery(id+"F0.wireOp",EDGE,"E10.3.0.0"),sQuery(id+"F0.wireOp",EDGE,"E10.4.0.0"),sQuery(id+"F0.wireOp",EDGE,"E10.5.0.0"),sQuery(id+"F0.wireOp",EDGE,"E10.6.0.0"),sQuery(id+"F0.wireOp",EDGE,"E10.7.0.0"),sQuery(id+"F0.wireOp",EDGE,"E11"),sQuery(id+"F0.wireOp",EDGE,"E12.1.0.0"),sQuery(id+"F0.wireOp",EDGE,"E12.2.0.0"),sQuery(id+"F0.wireOp",EDGE,"E12.3.0.0"),sQuery(id+"F0.wireOp",EDGE,"E12.4.0.0"),sQuery(id+"F0.wireOp",EDGE,"E12.5.0.0"),sQuery(id+"F0.wireOp",EDGE,"E12.6.0.0"),sQuery(id+"F0.wireOp",EDGE,"E12.7.0.0"),sQuery(id+"F0.wireOp",EDGE,"E12.8.0.0"),sQuery(id+"F0.wireOp",EDGE,"E12.9.0.0"),sQuery(id+"F0.wireOp",EDGE,"E14"),sQuery(id+"F0.wireOp",EDGE,"E15.1.0.0"),sQuery(id+"F0.wireOp",EDGE,"E15.2.0.0"),sQuery(id+"F0.wireOp",EDGE,"E15.3.0.0"),sQuery(id+"F0.wireOp",EDGE,"E15.4.0.0"),sQuery(id+"F0.wireOp",EDGE,"E15.5.0.0"),sQuery(id+"F0.wireOp",EDGE,"E16"),sQuery(id+"F0.wireOp",EDGE,"E17.1.0.0"),sQuery(id+"F0.wireOp",EDGE,"E17.2.0.0"),sQuery(id+"F0.wireOp",EDGE,"E17.3.0.0"),sQuery(id+"F0.wireOp",EDGE,"E17.4.0.0"),sQuery(id+"F0.wireOp",EDGE,"E17.5.0.0"),sQuery(id+"F0.wireOp",EDGE,"E17.6.0.0"),sQuery(id+"F0.wireOp",EDGE,"E17.7.0.0"),sQuery(id+"F0.wireOp",EDGE,"E19.1.0.2"),sQuery(id+"F0.wireOp",EDGE,"E19.1.0.3"),sQuery(id+"F0.wireOp",EDGE,"E19.1.0.4"),sQuery(id+"F0.wireOp",EDGE,"E19.1.0.6"),sQuery(id+"F0.wireOp",EDGE,"E19.1.0.7"),sQuery(id+"F0.wireOp",EDGE,"E19.1.0.8"),sQuery(id+"F0.wireOp",EDGE,"E19.1.0.9"),sQuery(id+"F0.wireOp",EDGE,"E19.1.0.10"),sQuery(id+"F0.wireOp",EDGE,"E19.1.0.11"),sQuery(id+"F0.wireOp",EDGE,"E19.1.0.12"),sQuery(id+"F0.wireOp",EDGE,"E19.1.0.13"),sQuery(id+"F0.wireOp",EDGE,"E19.1.0.14"),sQuery(id+"F0.wireOp",EDGE,"E19.1.0.15"),sQuery(id+"F0.wireOp",EDGE,"E19.1.0.16"),sQuery(id+"F0.wireOp",EDGE,"E19.1.0.17"),sQuery(id+"F0.wireOp",EDGE,"E19.1.0.18"),sQuery(id+"F0.wireOp",EDGE,"E19.1.0.19"),sQuery(id+"F0.wireOp",EDGE,"E21.1.0.1"),sQuery(id+"F0.wireOp",EDGE,"E21.1.0.2"),sQuery(id+"F0.wireOp",EDGE,"E21.1.0.3"),sQuery(id+"F0.wireOp",EDGE,"E21.1.0.4"),sQuery(id+"F0.wireOp",EDGE,"E21.1.0.5"),sQuery(id+"F0.wireOp",EDGE,"E21.1.0.6"),sQuery(id+"F0.wireOp",EDGE,"E21.1.0.7"),sQuery(id+"F0.wireOp",EDGE,"E21.1.0.8"),sQuery(id+"F0.wireOp",EDGE,"E21.1.0.9"),sQuery(id+"F0.wireOp",EDGE,"E21.1.0.10"),sQuery(id+"F0.wireOp",EDGE,"E21.1.0.11"),sQuery(id+"F0.wireOp",EDGE,"E21.1.0.12"),sQuery(id+"F0.wireOp",EDGE,"E25"),sQuery(id+"F0.wireOp",EDGE,"E26"),sQuery(id+"F0.wireOp",EDGE,"E27"),sQuery(id+"F0.wireOp",EDGE,"E28"),sQuery(id+"F0.wireOp",EDGE,"E29"),sQuery(id+"F0.wireOp",EDGE,"E30"),sQuery(id+"F0.wireOp",EDGE,"E31.1.0.0"),sQuery(id+"F0.wireOp",EDGE,"E31.1.0.1"),sQuery(id+"F0.wireOp",EDGE,"E31.1.0.2"),sQuery(id+"F0.wireOp",EDGE,"E31.1.0.3"),sQuery(id+"F0.wireOp",EDGE,"E31.1.0.4"),sQuery(id+"F0.wireOp",EDGE,"E31.1.0.5"),sQuery(id+"F0.wireOp",EDGE,"E31.2.0.0"),sQuery(id+"F0.wireOp",EDGE,"E31.2.0.1"),sQuery(id+"F0.wireOp",EDGE,"E31.2.0.2"),sQuery(id+"F0.wireOp",EDGE,"E31.2.0.3"),sQuery(id+"F0.wireOp",EDGE,"E31.2.0.4"),sQuery(id+"F0.wireOp",EDGE,"E31.2.0.5"),sQuery(id+"F0.wireOp",EDGE,"E31.3.0.0"),sQuery(id+"F0.wireOp",EDGE,"E31.3.0.1"),sQuery(id+"F0.wireOp",EDGE,"E31.3.0.2"),sQuery(id+"F0.wireOp",EDGE,"E31.3.0.3"),sQuery(id+"F0.wireOp",EDGE,"E31.3.0.4"),sQuery(id+"F0.wireOp",EDGE,"E31.3.0.5"),sQuery(id+"F0.wireOp",EDGE,"E31.4.0.0"),sQuery(id+"F0.wireOp",EDGE,"E31.4.0.1"),sQuery(id+"F0.wireOp",EDGE,"E31.4.0.2"),sQuery(id+"F0.wireOp",EDGE,"E31.4.0.3"),sQuery(id+"F0.wireOp",EDGE,"E31.4.0.4"),sQuery(id+"F0.wireOp",EDGE,"E31.4.0.5"),sQuery(id+"F0.wireOp",EDGE,"E31.5.0.0"),sQuery(id+"F0.wireOp",EDGE,"E31.5.0.1"),sQuery(id+"F0.wireOp",EDGE,"E31.5.0.2"),sQuery(id+"F0.wireOp",EDGE,"E31.5.0.3"),sQuery(id+"F0.wireOp",EDGE,"E31.5.0.4"),sQuery(id+"F0.wireOp",EDGE,"E31.5.0.5"),sQuery(id+"F0.wireOp",EDGE,"E31.6.0.0"),sQuery(id+"F0.wireOp",EDGE,"E31.6.0.1"),sQuery(id+"F0.wireOp",EDGE,"E31.6.0.2"),sQuery(id+"F0.wireOp",EDGE,"E31.6.0.3"),sQuery(id+"F0.wireOp",EDGE,"E31.6.0.4"),sQuery(id+"F0.wireOp",EDGE,"E31.6.0.5"),sQuery(id+"F0.wireOp",EDGE,"E31.7.0.0"),sQuery(id+"F0.wireOp",EDGE,"E31.7.0.1"),sQuery(id+"F0.wireOp",EDGE,"E31.7.0.2"),sQuery(id+"F0.wireOp",EDGE,"E31.7.0.3"),sQuery(id+"F0.wireOp",EDGE,"E31.7.0.4"),sQuery(id+"F0.wireOp",EDGE,"E31.7.0.5"),sQuery(id+"F0.wireOp",EDGE,"E31.8.0.0"),sQuery(id+"F0.wireOp",EDGE,"E31.8.0.1"),sQuery(id+"F0.wireOp",EDGE,"E31.8.0.2"),sQuery(id+"F0.wireOp",EDGE,"E31.8.0.3"),sQuery(id+"F0.wireOp",EDGE,"E31.8.0.4"),sQuery(id+"F0.wireOp",EDGE,"E31.8.0.5"),sQuery(id+"F0.wireOp",EDGE,"E31.9.0.0"),sQuery(id+"F0.wireOp",EDGE,"E31.9.0.1"),sQuery(id+"F0.wireOp",EDGE,"E31.9.0.2"),sQuery(id+"F0.wireOp",EDGE,"E31.9.0.3"),sQuery(id+"F0.wireOp",EDGE,"E31.9.0.4"),sQuery(id+"F0.wireOp",EDGE,"E31.9.0.5"),sQuery(id+"F0.wireOp",EDGE,"E31.10.0.0"),sQuery(id+"F0.wireOp",EDGE,"E31.10.0.1"),sQuery(id+"F0.wireOp",EDGE,"E31.10.0.2"),sQuery(id+"F0.wireOp",EDGE,"E31.10.0.3"),sQuery(id+"F0.wireOp",EDGE,"E31.10.0.4"),sQuery(id+"F0.wireOp",EDGE,"E31.10.0.5"),sQuery(id+"F0.wireOp",EDGE,"E31.11.0.0"),sQuery(id+"F0.wireOp",EDGE,"E31.11.0.1"),sQuery(id+"F0.wireOp",EDGE,"E31.11.0.2"),sQuery(id+"F0.wireOp",EDGE,"E31.11.0.3"),sQuery(id+"F0.wireOp",EDGE,"E31.11.0.4"),sQuery(id+"F0.wireOp",EDGE,"E31.11.0.5"),sQuery(id+"F0.wireOp",EDGE,"E31.12.0.0"),sQuery(id+"F0.wireOp",EDGE,"E31.12.0.1"),sQuery(id+"F0.wireOp",EDGE,"E31.12.0.2"),sQuery(id+"F0.wireOp",EDGE,"E31.12.0.3"),sQuery(id+"F0.wireOp",EDGE,"E31.12.0.4"),sQuery(id+"F0.wireOp",EDGE,"E31.12.0.5"),sQuery(id+"F0.wireOp",EDGE,"E31.13.0.0"),sQuery(id+"F0.wireOp",EDGE,"E31.13.0.1"),sQuery(id+"F0.wireOp",EDGE,"E31.13.0.2"),sQuery(id+"F0.wireOp",EDGE,"E31.13.0.3"),sQuery(id+"F0.wireOp",EDGE,"E31.13.0.4"),sQuery(id+"F0.wireOp",EDGE,"E31.13.0.5"),sQuery(id+"F0.wireOp",EDGE,"E31.14.0.0"),sQuery(id+"F0.wireOp",EDGE,"E31.14.0.1"),sQuery(id+"F0.wireOp",EDGE,"E31.14.0.2"),sQuery(id+"F0.wireOp",EDGE,"E31.14.0.3"),sQuery(id+"F0.wireOp",EDGE,"E31.14.0.4"),sQuery(id+"F0.wireOp",EDGE,"E31.14.0.5"),sQuery(id+"F0.wireOp",EDGE,"E31.15.0.0"),sQuery(id+"F0.wireOp",EDGE,"E31.15.0.1"),sQuery(id+"F0.wireOp",EDGE,"E31.15.0.2"),sQuery(id+"F0.wireOp",EDGE,"E31.15.0.3"),sQuery(id+"F0.wireOp",EDGE,"E31.15.0.4"),sQuery(id+"F0.wireOp",EDGE,"E31.15.0.5"),sQuery(id+"F0.wireOp",EDGE,"E31.16.0.0"),sQuery(id+"F0.wireOp",EDGE,"E31.16.0.1"),sQuery(id+"F0.wireOp",EDGE,"E31.16.0.2"),sQuery(id+"F0.wireOp",EDGE,"E31.16.0.3"),sQuery(id+"F0.wireOp",EDGE,"E31.16.0.4"),sQuery(id+"F0.wireOp",EDGE,"E31.16.0.5"),sQuery(id+"F0.wireOp",EDGE,"E31.17.0.0"),sQuery(id+"F0.wireOp",EDGE,"E31.17.0.1"),sQuery(id+"F0.wireOp",EDGE,"E31.17.0.2"),sQuery(id+"F0.wireOp",EDGE,"E31.17.0.3"),sQuery(id+"F0.wireOp",EDGE,"E31.17.0.4"),sQuery(id+"F0.wireOp",EDGE,"E31.17.0.5"),sQuery(id+"F0.wireOp",EDGE,"E31.18.0.0"),sQuery(id+"F0.wireOp",EDGE,"E31.18.0.1"),sQuery(id+"F0.wireOp",EDGE,"E31.18.0.2"),sQuery(id+"F0.wireOp",EDGE,"E31.18.0.3"),sQuery(id+"F0.wireOp",EDGE,"E31.18.0.4"),sQuery(id+"F0.wireOp",EDGE,"E31.18.0.5"),sQuery(id+"F0.wireOp",EDGE,"E32"),sQuery(id+"F0.wireOp",EDGE,"E33"),sQuery(id+"F0.wireOp",EDGE,"E34"),sQuery(id+"F0.wireOp",EDGE,"E36"),sQuery(id+"F0.wireOp",EDGE,"E37"),sQuery(id+"F0.wireOp",EDGE,"E38"),sQuery(id+"F0.wireOp",EDGE,"E39"),sQuery(id+"F0.wireOp",EDGE,"E40"),sQuery(id+"F0.wireOp",EDGE,"E41"),sQuery(id+"F0.wireOp",EDGE,"E42"),sQuery(id+"F0.wireOp",EDGE,"E43"),sQuery(id+"F0.wireOp",EDGE,"E44"),sQuery(id+"F0.wireOp",EDGE,"E45.bottom"),sQuery(id+"F0.wireOp",EDGE,"E45.top"),sQuery(id+"F0.wireOp",EDGE,"E45.left"),sQuery(id+"F0.wireOp",EDGE,"E45.right"),sQuery(id+"F0.wireOp",EDGE,"E46.bottom"),sQuery(id+"F0.wireOp",EDGE,"E46.top"),sQuery(id+"F0.wireOp",EDGE,"E46.left"),sQuery(id+"F0.wireOp",EDGE,"E46.right"),sQuery(id+"F0.wireOp",EDGE,"E47.bottom"),sQuery(id+"F0.wireOp",EDGE,"E47.top"),sQuery(id+"F0.wireOp",EDGE,"E47.left"),sQuery(id+"F0.wireOp",EDGE,"E47.right"),sQuery(id+"F0.wireOp",EDGE,"E56"),sQuery(id+"F0.wireOp",EDGE,"E57"),sQuery(id+"F0.wireOp",EDGE,"E58"),sQuery(id+"F0.wireOp",EDGE,"E59"),sQuery(id+"F0.wireOp",EDGE,"E60"),sQuery(id+"F0.wireOp",EDGE,"E69"),sQuery(id+"F0.wireOp",EDGE,"E70"),sQuery(id+"F0.wireOp",EDGE,"E71"),sQuery(id+"F0.wireOp",EDGE,"E72"),sQuery(id+"F0.wireOp",EDGE,"E73"),sQuery(id+"F0.wireOp",EDGE,"E79"),sQuery(id+"F0.wireOp",EDGE,"E80"),sQuery(id+"F0.wireOp",EDGE,"E85.bottom"),sQuery(id+"F0.wireOp",EDGE,"E85.top"),sQuery(id+"F0.wireOp",EDGE,"E85.left"),sQuery(id+"F0.wireOp",EDGE,"E85.right"),sQuery(id+"F0.wireOp",EDGE,"E86.bottom"),sQuery(id+"F0.wireOp",EDGE,"E86.top"),sQuery(id+"F0.wireOp",EDGE,"E86.left"),sQuery(id+"F0.wireOp",EDGE,"E86.right"),sQuery(id+"F0.wireOp",EDGE,"E87.bottom"),sQuery(id+"F0.wireOp",EDGE,"E87.top"),sQuery(id+"F0.wireOp",EDGE,"E87.left"),sQuery(id+"F0.wireOp",EDGE,"E87.right"),sQuery(id+"F0.wireOp",EDGE,"E88.bottom"),sQuery(id+"F0.wireOp",EDGE,"E88.top"),sQuery(id+"F0.wireOp",EDGE,"E88.left"),sQuery(id+"F0.wireOp",EDGE,"E88.right"),sQuery(id+"F0.wireOp",EDGE,"E89.bottom"),sQuery(id+"F0.wireOp",EDGE,"E89.top"),sQuery(id+"F0.wireOp",EDGE,"E89.left"),sQuery(id+"F0.wireOp",EDGE,"E89.right"),sQuery(id+"F0.wireOp",EDGE,"E90.bottom"),sQuery(id+"F0.wireOp",EDGE,"E90.top"),sQuery(id+"F0.wireOp",EDGE,"E90.left"),sQuery(id+"F0.wireOp",EDGE,"E90.right"),sQuery(id+"F0.wireOp",EDGE,"E92.bottom"),sQuery(id+"F0.wireOp",EDGE,"E92.top"),sQuery(id+"F0.wireOp",EDGE,"E92.left"),sQuery(id+"F0.wireOp",EDGE,"E92.right"),sQuery(id+"F0.wireOp",EDGE,"E93.bottom"),sQuery(id+"F0.wireOp",EDGE,"E93.top"),sQuery(id+"F0.wireOp",EDGE,"E93.left"),sQuery(id+"F0.wireOp",EDGE,"E93.right")])],"isStart":false});
            var sketch = newSketch(context, id + "F6", { "sketchPlane" : qUnion([Q0])});
            skLineSegment(sketch, "E291.bottom", {"start": v(2.7, 38.24) * mm, "end": v(9, 38.24) * mm});
            skLineSegment(sketch, "E291.top", {"start": v(2.7, 32.34) * mm, "end": v(9, 32.34) * mm});
            skLineSegment(sketch, "E291.left", {"start": v(2.7, 38.24) * mm, "end": v(2.7, 32.34) * mm});
            skLineSegment(sketch, "E291.right", {"start": v(9, 38.24) * mm, "end": v(9, 32.34) * mm});
            skLineSegment(sketch, "E292.bottom", {"start": v(1.7, 11.7) * mm, "end": v(8.5, 11.7) * mm});
            skLineSegment(sketch, "E292.top", {"start": v(1.7, 5.4) * mm, "end": v(8.5, 5.4) * mm});
            skLineSegment(sketch, "E292.left", {"start": v(1.7, 11.7) * mm, "end": v(1.7, 5.4) * mm});
            skLineSegment(sketch, "E292.right", {"start": v(8.5, 11.7) * mm, "end": v(8.5, 5.4) * mm});
            skSolve(sketch);
        }
        {
            var Q0;
            Q0 = qSketchRegion(id + "F6", true);
            extrude(context, id + "F7", {"entities" : qUnion([Q0]), "operationType" : NewBodyOperationType.REMOVE, "oppositeDirection" : true, "depth" : 0.2 * mm});
        }
    });
